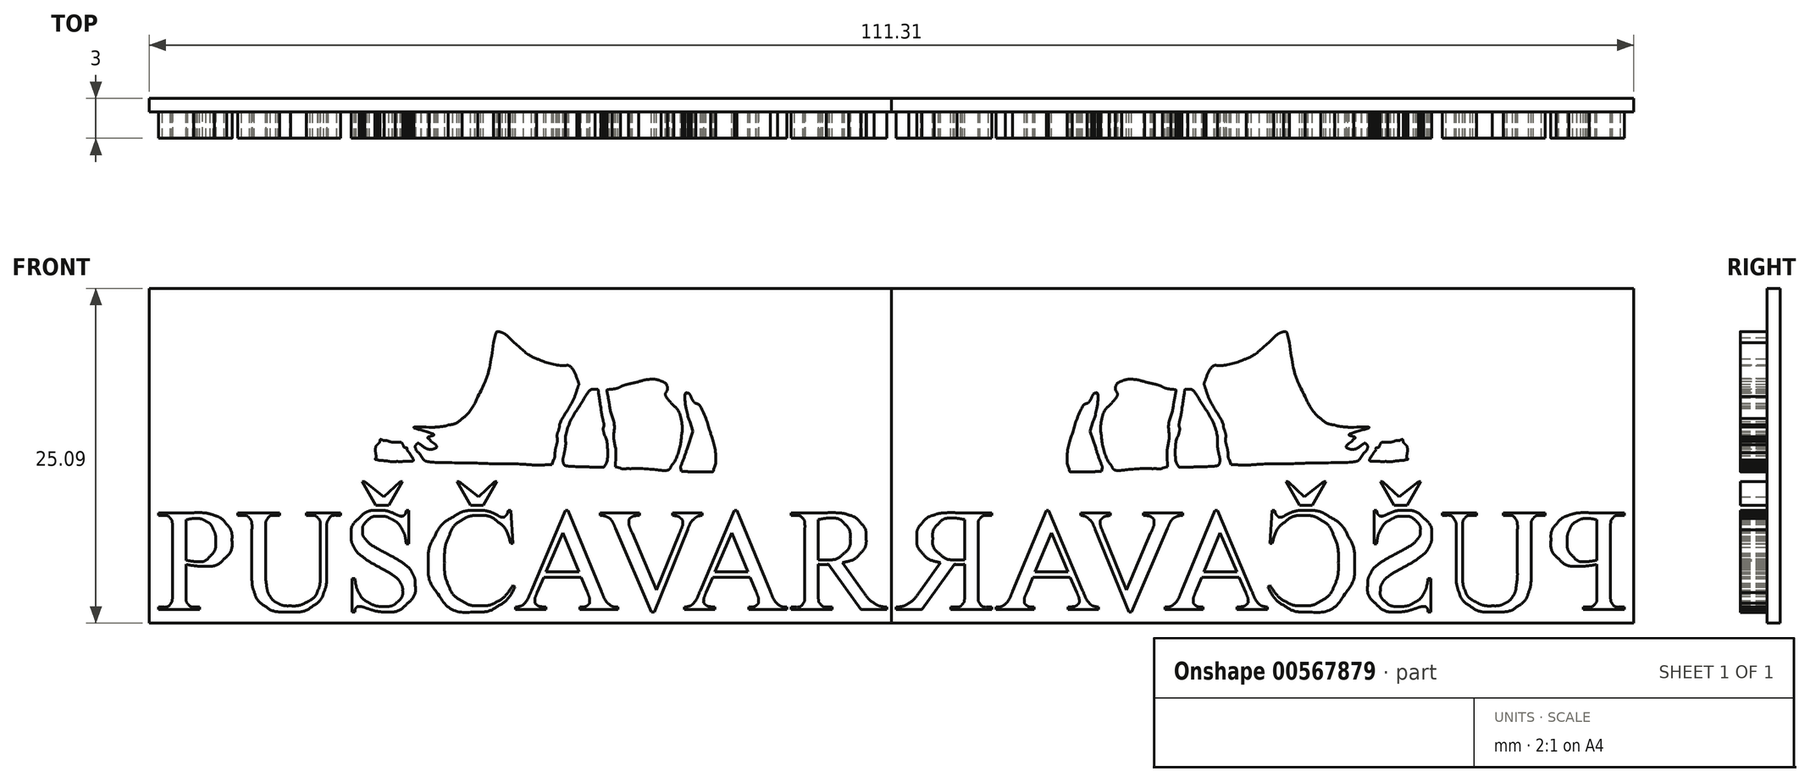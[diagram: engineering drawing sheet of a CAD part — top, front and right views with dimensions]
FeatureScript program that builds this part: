
annotation { "Feature Type Name" : "Feature", "Feature Type Description" : "" }
export const myFeature = defineFeature(function(context is Context, id is Id, definition is map)
    precondition{}
    {
        {
            var Q0;
            Q0=qCreatedBy(makeId("Front.planeOp"),FACE);
            var sketch = newSketch(context, id + "F0", { "sketchPlane" : qUnion([Q0])});
            skFitSpline(sketch, "E0", {"points": [v(14.9, -1.88) * mm, v(14.32, -1.78) * mm, v(13.15, -1.72) * mm, v(11.14, -1.7) * mm]});
            skFitSpline(sketch, "E1", {"points": [v(11.14, -1.7) * mm, v(9.53, -1.67) * mm, v(7.75, -1.61) * mm, v(7.18, -1.56) * mm]});
            skFitSpline(sketch, "E2", {"points": [v(7.18, -1.56) * mm, v(6.6, -1.5) * mm, v(4.27, -1.44) * mm, v(2, -1.41) * mm]});
            skFitSpline(sketch, "E3", {"points": [v(2, -1.41) * mm, v(-0.29, -1.38) * mm, v(-2.6, -1.32) * mm, v(-3.16, -1.26) * mm]});
            skFitSpline(sketch, "E4", {"points": [v(-3.16, -1.26) * mm, v(-3.72, -1.21) * mm, v(-6.43, -1.21) * mm, v(-9.2, -1.18) * mm]});
            skFitSpline(sketch, "E5", {"points": [v(-9.2, -1.18) * mm, v(-13.82, -1.47) * mm, v(-16.55, -0.57) * mm, v(-17.95, 0.52) * mm]});
            skFitSpline(sketch, "E6", {"points": [v(-17.95, 0.52) * mm, v(-20.19, 1.8) * mm, v(-20.67, 2.48) * mm, v(-22.93, 2.6) * mm]});
            skFitSpline(sketch, "E7", {"points": [v(-22.93, 2.6) * mm, v(-24.75, 2.6) * mm, v(-25.04, 2.34) * mm, v(-27, 1.58) * mm]});
            skFitSpline(sketch, "E8", {"points": [v(-27, 1.58) * mm, v(-25.87, 2.73) * mm, v(-24.51, 3.06) * mm, v(-22.9, 3.24) * mm]});
            skFitSpline(sketch, "E9", {"points": [v(-22.9, 3.24) * mm, v(-20.45, 3.27) * mm, v(-17.5, 1.3) * mm, v(-15.9, 0.65) * mm]});
            skFitSpline(sketch, "E10", {"points": [v(-15.9, 0.65) * mm, v(-14.3, 0) * mm, v(-13.89, 0.1) * mm, v(-12.91, -0.13) * mm]});
            skFitSpline(sketch, "E11", {"points": [v(-12.91, -0.13) * mm, v(-12.7, -0.19) * mm, v(-11.86, -0.25) * mm, v(-11.73, -0.1) * mm]});
            skFitSpline(sketch, "E12", {"points": [v(-11.73, -0.1) * mm, v(-11.64, 0) * mm, v(-11.63, 0.35) * mm, v(-11.68, 1.18) * mm]});
            skFitSpline(sketch, "E13", {"points": [v(-11.68, 1.18) * mm, v(-11.74, 2.22) * mm, v(-11.73, 2.38) * mm, v(-11.53, 3) * mm]});
            skFitSpline(sketch, "E14", {"points": [v(-11.53, 3) * mm, v(-11.4, 3.37) * mm, v(-11.14, 4.02) * mm, v(-10.93, 4.43) * mm]});
            skFitSpline(sketch, "E15", {"points": [v(-10.69, 5.94) * mm, v(-10.76, 6.36) * mm, v(-10.82, 7.09) * mm, v(-10.81, 7.57) * mm]});
            skFitSpline(sketch, "E16", {"points": [v(-10.81, 7.57) * mm, v(-10.8, 8.41) * mm, v(-10.81, 8.44) * mm, v(-11.02, 8.44) * mm]});
            skFitSpline(sketch, "E17", {"points": [v(-11.02, 8.44) * mm, v(-11.17, 8.44) * mm, v(-11.28, 8.55) * mm, v(-11.43, 8.86) * mm]});
            skFitSpline(sketch, "E18", {"points": [v(-11.43, 8.86) * mm, v(-11.54, 9.1) * mm, v(-11.63, 9.34) * mm, v(-11.63, 9.41) * mm]});
            skFitSpline(sketch, "E19", {"points": [v(-11.63, 9.41) * mm, v(-11.63, 9.56) * mm, v(-11.28, 9.9) * mm, v(-11.03, 9.98) * mm]});
            skFitSpline(sketch, "E20", {"points": [v(-11.03, 9.98) * mm, v(-10.63, 10.12) * mm, v(-10.18, 9.52) * mm, v(-10.28, 8.99) * mm]});
            skFitSpline(sketch, "E21", {"points": [v(-10.28, 8.99) * mm, v(-10.32, 8.78) * mm, v(-10.25, 8.66) * mm, v(-9.86, 8.3) * mm]});
            skFitSpline(sketch, "E22", {"points": [v(-9.86, 8.3) * mm, v(-9.2, 7.7) * mm, v(-8.6, 6.3) * mm, v(-8.75, 5.8) * mm]});
            skFitSpline(sketch, "E23", {"points": [v(-8.75, 5.8) * mm, v(-8.79, 5.7) * mm, v(-8.77, 5.61) * mm, v(-8.72, 5.61) * mm]});
            skFitSpline(sketch, "E24", {"points": [v(-8.72, 5.61) * mm, v(-8.67, 5.61) * mm, v(-8.57, 5.38) * mm, v(-8.5, 5.08) * mm]});
            skFitSpline(sketch, "E25", {"points": [v(-8.5, 5.08) * mm, v(-8.44, 4.8) * mm, v(-8.26, 4.37) * mm, v(-8.1, 4.14) * mm]});
            skFitSpline(sketch, "E26", {"points": [v(-8.1, 4.14) * mm, v(-7.95, 3.9) * mm, v(-7.8, 3.58) * mm, v(-7.77, 3.42) * mm]});
            skFitSpline(sketch, "E27", {"points": [v(-7.77, 3.42) * mm, v(-7.72, 3.17) * mm, v(-7.62, 3.13) * mm, v(-7.13, 2.94) * mm]});
            skFitSpline(sketch, "E28", {"points": [v(-7.13, 2.94) * mm, v(-6.82, 2.82) * mm, v(-6.27, 2.96) * mm, v(-6, 2.99) * mm]});
            skFitSpline(sketch, "E29", {"points": [v(-6, 2.99) * mm, v(-5.6, 3.02) * mm, v(-4.84, 3.2) * mm, v(-4.06, 4.8) * mm]});
            skFitSpline(sketch, "E30", {"points": [v(-4.06, 4.8) * mm, v(-3.61, 5.73) * mm, v(-3.42, 6.24) * mm, v(-3.16, 6.99) * mm]});
            skFitSpline(sketch, "E31", {"points": [v(-3.16, 6.99) * mm, v(-2.96, 7.56) * mm, v(-2.8, 8.36) * mm, v(-2.73, 8.7) * mm]});
            skFitSpline(sketch, "E32", {"points": [v(-2.73, 8.7) * mm, v(-2.52, 9.68) * mm, v(-2.41, 9.64) * mm, v(-2.93, 9.69) * mm]});
            skFitSpline(sketch, "E33", {"points": [v(-2.93, 9.69) * mm, v(-3.18, 9.71) * mm, v(-3.48, 9.68) * mm, v(-3.61, 9.61) * mm]});
            skFitSpline(sketch, "E34", {"points": [v(-3.61, 9.61) * mm, v(-3.78, 9.53) * mm, v(-3.9, 9.53) * mm, v(-4.06, 9.6) * mm]});
            skFitSpline(sketch, "E35", {"points": [v(-4.06, 9.6) * mm, v(-4.25, 9.68) * mm, v(-4.27, 9.75) * mm, v(-4.22, 9.99) * mm]});
            skFitSpline(sketch, "E36", {"points": [v(-4.22, 9.99) * mm, v(-4.19, 10.15) * mm, v(-4.12, 10.34) * mm, v(-4.08, 10.42) * mm]});
            skFitSpline(sketch, "E37", {"points": [v(-4.08, 10.42) * mm, v(-3.99, 10.6) * mm, v(-3.04, 11.08) * mm, v(-2.77, 11.08) * mm]});
            skFitSpline(sketch, "E38", {"points": [v(-2.77, 11.08) * mm, v(-2.67, 11.08) * mm, v(-2.42, 11.16) * mm, v(-2.23, 11.27) * mm]});
            skFitSpline(sketch, "E39", {"points": [v(-2.23, 11.27) * mm, v(-1.47, 11.66) * mm, v(-1.37, 11.63) * mm, v(-0.75, 10.87) * mm]});
            skFitSpline(sketch, "E40", {"points": [v(-0.75, 10.87) * mm, v(-0.1, 10.05) * mm, v(0.8, 9.25) * mm, v(1.27, 9.04) * mm]});
            skFitSpline(sketch, "E41", {"points": [v(1.27, 9.04) * mm, v(2.05, 8.7) * mm, v(3.56, 8.93) * mm, v(4.48, 9.53) * mm]});
            skFitSpline(sketch, "E42", {"points": [v(4.48, 9.53) * mm, v(5.16, 9.98) * mm, v(6.19, 11.05) * mm, v(6.25, 11.39) * mm]});
            skFitSpline(sketch, "E43", {"points": [v(6.25, 11.39) * mm, v(6.32, 11.74) * mm, v(6.58, 11.72) * mm, v(6.9, 11.35) * mm]});
            skFitSpline(sketch, "E44", {"points": [v(6.9, 11.35) * mm, v(7.1, 11.1) * mm, v(7.18, 11.06) * mm, v(7.32, 11.15) * mm]});
            skFitSpline(sketch, "E45", {"points": [v(7.32, 11.15) * mm, v(7.43, 11.22) * mm, v(7.88, 11.24) * mm, v(8.7, 11.2) * mm]});
            skFitSpline(sketch, "E46", {"points": [v(8.7, 11.2) * mm, v(9.75, 11.15) * mm, v(9.93, 11.17) * mm, v(10.04, 11.3) * mm]});
            skFitSpline(sketch, "E47", {"points": [v(10.04, 11.3) * mm, v(10.28, 11.59) * mm, v(10.71, 11.43) * mm, v(10.71, 11.06) * mm]});
            skFitSpline(sketch, "E48", {"points": [v(10.71, 11.06) * mm, v(10.71, 10.96) * mm, v(10.81, 10.84) * mm, v(10.93, 10.79) * mm]});
            skFitSpline(sketch, "E49", {"points": [v(10.93, 10.79) * mm, v(11.06, 10.73) * mm, v(11.23, 10.54) * mm, v(11.31, 10.36) * mm]});
            skFitSpline(sketch, "E50", {"points": [v(11.31, 10.36) * mm, v(11.4, 10.18) * mm, v(11.65, 9.83) * mm, v(11.87, 9.6) * mm]});
            skFitSpline(sketch, "E51", {"points": [v(11.87, 9.6) * mm, v(12.53, 8.88) * mm, v(12.96, 8.21) * mm, v(13.3, 7.42) * mm]});
            skFitSpline(sketch, "E52", {"points": [v(13.3, 7.42) * mm, v(13.58, 6.8) * mm, v(13.65, 6.49) * mm, v(13.73, 5.57) * mm]});
            skFitSpline(sketch, "E53", {"points": [v(13.73, 5.57) * mm, v(13.8, 4.85) * mm, v(13.88, 4.35) * mm, v(14, 4.12) * mm]});
            skFitSpline(sketch, "E54", {"points": [v(14, 4.12) * mm, v(14.1, 3.93) * mm, v(14.22, 3.56) * mm, v(14.33, 3.35) * mm]});
            skFitSpline(sketch, "E55", {"points": [v(14.33, 3.35) * mm, v(14.44, 3.11) * mm, v(14.48, 2.89) * mm, v(14.58, 2.72) * mm]});
            skFitSpline(sketch, "E56", {"points": [v(14.58, 2.72) * mm, v(14.74, 2.46) * mm, v(14.75, 2.1) * mm, v(14.95, 1.13) * mm]});
            skFitSpline(sketch, "E57", {"points": [v(14.95, 1.13) * mm, v(15.08, 0.48) * mm, v(15, -0.27) * mm, v(15.09, -0.62) * mm]});
            skLineSegment(sketch, "E58", {"start": v(-10.93, 4.43) * mm, "end": v(-10.56, 5.19) * mm});
            skLineSegment(sketch, "E59", {"start": v(-10.56, 5.19) * mm, "end": v(-10.69, 5.94) * mm});
            skFitSpline(sketch, "E60", {"points": [v(15.75, -1.16) * mm, v(16.12, -1.2) * mm, v(16.68, -1.18) * mm, v(17.24, -1.22) * mm]});
            skFitSpline(sketch, "E61", {"points": [v(17.24, -1.22) * mm, v(17.96, -1.27) * mm, v(18.5, -1.26) * mm, v(19.08, -1.17) * mm]});
            skFitSpline(sketch, "E62", {"points": [v(19.08, -1.17) * mm, v(19.84, -1.05) * mm, v(20.1, -0.95) * mm, v(22.27, 0.16) * mm]});
            skFitSpline(sketch, "E63", {"points": [v(22.27, 0.16) * mm, v(24.47, 1.27) * mm, v(26.34, 2.02) * mm, v(26.66, 1.92) * mm]});
            skFitSpline(sketch, "E64", {"points": [v(26.66, 1.92) * mm, v(25.58, 1.3) * mm, v(25.17, 1.06) * mm, v(24.85, 0.96) * mm]});
            skFitSpline(sketch, "E65", {"points": [v(24.85, 0.96) * mm, v(24.04, 0.58) * mm, v(23.13, 0.07) * mm, v(21.22, -0.88) * mm]});
            skFitSpline(sketch, "E66", {"points": [v(21.22, -0.88) * mm, v(19, -2) * mm, v(18.7, -1.79) * mm, v(17.93, -1.92) * mm]});
            skFitSpline(sketch, "E67", {"points": [v(17.93, -1.92) * mm, v(17.12, -1.92) * mm, v(15.47, -1.91) * mm, v(14.9, -1.88) * mm]});
            skLineSegment(sketch, "E68", {"start": v(15.09, -0.62) * mm, "end": v(15.2, -1.1) * mm});
            skLineSegment(sketch, "E69", {"start": v(15.2, -1.1) * mm, "end": v(15.75, -1.16) * mm});
            skFitSpline(sketch, "E70", {"points": [v(14.33, -0.94) * mm, v(14.48, -0.39) * mm, v(14.38, 0.8) * mm, v(14.11, 1.68) * mm]});
            skFitSpline(sketch, "E71", {"points": [v(14.11, 1.68) * mm, v(13.79, 2.73) * mm, v(13.24, 3.87) * mm, v(12.99, 4) * mm]});
            skFitSpline(sketch, "E72", {"points": [v(12.99, 4) * mm, v(12.89, 4.06) * mm, v(12.74, 4.25) * mm, v(12.65, 4.43) * mm]});
            skFitSpline(sketch, "E73", {"points": [v(12.65, 4.43) * mm, v(12.57, 4.61) * mm, v(12.45, 4.76) * mm, v(12.4, 4.76) * mm]});
            skFitSpline(sketch, "E74", {"points": [v(12.4, 4.76) * mm, v(12.22, 4.76) * mm, v(12.3, 3.38) * mm, v(12.54, 2.64) * mm]});
            skLineSegment(sketch, "E75", {"start": v(14.9, -1.88) * mm, "end": v(14.9, -1.88) * mm});
            skFitSpline(sketch, "E76", {"points": [v(12.34, 0.63) * mm, v(12.1, -0.1) * mm, v(11.87, -0.68) * mm, v(11.84, -0.82) * mm]});
            skLineSegment(sketch, "E77", {"start": v(12.54, 2.64) * mm, "end": v(12.77, 1.93) * mm});
            skLineSegment(sketch, "E78", {"start": v(12.77, 1.93) * mm, "end": v(12.34, 0.63) * mm});
            skFitSpline(sketch, "E79", {"points": [v(12.1, -1.1) * mm, v(12.45, -1.12) * mm, v(13.09, -1.13) * mm, v(13.51, -1.13) * mm]});
            skFitSpline(sketch, "E80", {"points": [v(13.51, -1.13) * mm, v(14.2, -1.13) * mm, v(14.29, -1.1) * mm, v(14.33, -0.94) * mm]});
            skLineSegment(sketch, "E81", {"start": v(11.84, -0.82) * mm, "end": v(11.9, -1.09) * mm});
            skLineSegment(sketch, "E82", {"start": v(11.9, -1.09) * mm, "end": v(12.1, -1.1) * mm});
            skFitSpline(sketch, "E83", {"points": [v(10.97, -0.97) * mm, v(11.07, -0.87) * mm, v(11.12, -0.73) * mm, v(11.22, -0.59) * mm]});
            skFitSpline(sketch, "E84", {"points": [v(11.22, -0.59) * mm, v(11.48, -0.2) * mm, v(11.84, 0.92) * mm, v(11.9, 1.53) * mm]});
            skFitSpline(sketch, "E85", {"points": [v(11.9, 1.53) * mm, v(11.97, 2.23) * mm, v(11.68, 3.45) * mm, v(11.35, 3.81) * mm]});
            skFitSpline(sketch, "E86", {"points": [v(11.35, 3.81) * mm, v(10.95, 4.25) * mm, v(10.7, 4.67) * mm, v(10.75, 4.82) * mm]});
            skFitSpline(sketch, "E87", {"points": [v(10.75, 4.82) * mm, v(10.87, 5.12) * mm, v(10.7, 5.54) * mm, v(10.4, 5.66) * mm]});
            skFitSpline(sketch, "E88", {"points": [v(10.4, 5.66) * mm, v(10.06, 5.79) * mm, v(9.26, 5.77) * mm, v(8.69, 5.62) * mm]});
            skFitSpline(sketch, "E89", {"points": [v(8.69, 5.62) * mm, v(8.48, 5.57) * mm, v(8.14, 5.5) * mm, v(7.93, 5.45) * mm]});
            skFitSpline(sketch, "E90", {"points": [v(7.93, 5.45) * mm, v(7.72, 5.4) * mm, v(7.45, 5.3) * mm, v(7.32, 5.24) * mm]});
            skFitSpline(sketch, "E91", {"points": [v(7.32, 5.24) * mm, v(7.2, 5.17) * mm, v(6.92, 5.1) * mm, v(6.7, 5.07) * mm]});
            skFitSpline(sketch, "E92", {"points": [v(6.7, 5.07) * mm, v(6.5, 5.05) * mm, v(6.33, 5.02) * mm, v(6.32, 5.01) * mm]});
            skFitSpline(sketch, "E93", {"points": [v(6.32, 5.01) * mm, v(6.32, 5) * mm, v(6.4, 4.53) * mm, v(6.5, 3.96) * mm]});
            skFitSpline(sketch, "E94", {"points": [v(6.5, 3.96) * mm, v(6.62, 3.3) * mm, v(6.86, 2.5) * mm, v(6.85, 1.84) * mm]});
            skFitSpline(sketch, "E95", {"points": [v(6.85, 1.84) * mm, v(6.84, 1.27) * mm, v(6.99, 0.5) * mm, v(6.98, 0.08) * mm]});
            skFitSpline(sketch, "E96", {"points": [v(7.32, -0.85) * mm, v(7.5, -0.91) * mm, v(7.71, -0.9) * mm, v(8.09, -0.9) * mm]});
            skFitSpline(sketch, "E97", {"points": [v(8.09, -0.9) * mm, v(9.03, -0.9) * mm, v(10.36, -1.01) * mm, v(10.44, -1.02) * mm]});
            skFitSpline(sketch, "E98", {"points": [v(10.44, -1.02) * mm, v(10.61, -1.05) * mm, v(10.81, -1.02) * mm, v(10.97, -0.97) * mm]});
            skLineSegment(sketch, "E99", {"start": v(6.98, 0.08) * mm, "end": v(6.96, -0.75) * mm});
            skLineSegment(sketch, "E100", {"start": v(6.96, -0.75) * mm, "end": v(7.32, -0.85) * mm});
            skFitSpline(sketch, "E101", {"points": [v(6.18, -0.61) * mm, v(6.33, -0.34) * mm, v(6.3, 1.2) * mm, v(6.15, 1.57) * mm]});
            skFitSpline(sketch, "E102", {"points": [v(6.15, 1.57) * mm, v(6.03, 2.13) * mm, v(6.05, 2.18) * mm, v(6.07, 2.22) * mm]});
            skFitSpline(sketch, "E103", {"points": [v(6.07, 2.22) * mm, v(6.11, 2.37) * mm, v(6.1, 2.38) * mm, v(6.09, 2.47) * mm]});
            skFitSpline(sketch, "E104", {"points": [v(6.09, 2.47) * mm, v(6.07, 2.56) * mm, v(5.95, 3.11) * mm, v(5.86, 3.68) * mm]});
            skFitSpline(sketch, "E105", {"points": [v(5.86, 3.68) * mm, v(5.67, 4.98) * mm, v(5.65, 5.05) * mm, v(5.44, 5.05) * mm]});
            skFitSpline(sketch, "E106", {"points": [v(5.44, 5.05) * mm, v(5.14, 5.05) * mm, v(4.83, 4.71) * mm, v(4.24, 3.76) * mm]});
            skFitSpline(sketch, "E107", {"points": [v(4.24, 3.76) * mm, v(3.64, 2.8) * mm, v(3.23, 1.61) * mm, v(3.22, 1.06) * mm]});
            skFitSpline(sketch, "E108", {"points": [v(3.22, 1.06) * mm, v(3.22, 0.9) * mm, v(3.16, 0.46) * mm, v(3.09, 0.1) * mm]});
            skFitSpline(sketch, "E109", {"points": [v(3.09, 0.1) * mm, v(3.02, -0.27) * mm, v(3.1, -0.59) * mm, v(3.12, -0.61) * mm]});
            skFitSpline(sketch, "E110", {"points": [v(3.12, -0.61) * mm, v(3.16, -0.66) * mm, v(4.56, -0.76) * mm, v(5.5, -0.78) * mm]});
            skFitSpline(sketch, "E111", {"points": [v(5.5, -0.78) * mm, v(6, -0.8) * mm, v(6.1, -0.77) * mm, v(6.18, -0.61) * mm]});
            skLineSegment(sketch, "E112", {"start": v(10.97, -0.97) * mm, "end": v(10.97, -0.97) * mm});
            skFitSpline(sketch, "E113", {"points": [v(-7.05, 1.5) * mm, v(-7.13, 1.4) * mm, v(-7, 1.33) * mm, v(-6.91, 1.18) * mm]});
            skFitSpline(sketch, "E114", {"points": [v(-6.91, 1.18) * mm, v(-6.44, 0.72) * mm, v(-7.06, 0.56) * mm, v(-7.58, 0.87) * mm]});
            skFitSpline(sketch, "E115", {"points": [v(-7.58, 0.87) * mm, v(-7.84, 1.03) * mm, v(-7.86, 1.03) * mm, v(-8.02, 0.87) * mm]});
            skFitSpline(sketch, "E116", {"points": [v(-8.02, 0.87) * mm, v(-8.06, 0.77) * mm, v(-8.05, 0.68) * mm, v(-8.03, 0.6) * mm]});
            skFitSpline(sketch, "E117", {"points": [v(-8.03, 0.6) * mm, v(-7.94, 0.42) * mm, v(-7.78, 0.28) * mm, v(-7.63, 0.08) * mm]});
            skFitSpline(sketch, "E118", {"points": [v(-7.63, 0.08) * mm, v(-7.44, -0.2) * mm, v(-7.3, -0.32) * mm, v(-7.04, -0.37) * mm]});
            skFitSpline(sketch, "E119", {"points": [v(-7.04, -0.37) * mm, v(-6.86, -0.4) * mm, v(-5.3, -0.45) * mm, v(-3.6, -0.47) * mm]});
            skFitSpline(sketch, "E120", {"points": [v(-3.6, -0.47) * mm, v(-2.4, -0.52) * mm, v(-0.8, -0.52) * mm, v(0.23, -0.58) * mm]});
            skFitSpline(sketch, "E121", {"points": [v(0.23, -0.58) * mm, v(0.87, -0.62) * mm, v(1.6, -0.61) * mm, v(2.18, -0.6) * mm]});
            skFitSpline(sketch, "E122", {"points": [v(2.33, -0.23) * mm, v(2.4, -0.04) * mm, v(2.44, 0.43) * mm, v(2.51, 0.8) * mm]});
            skFitSpline(sketch, "E123", {"points": [v(2.51, 0.8) * mm, v(2.6, 1.2) * mm, v(2.58, 1.6) * mm, v(2.66, 1.91) * mm]});
            skFitSpline(sketch, "E124", {"points": [v(2.66, 1.91) * mm, v(2.76, 2.28) * mm, v(2.76, 2.4) * mm, v(3.45, 3.63) * mm]});
            skFitSpline(sketch, "E125", {"points": [v(3.45, 3.63) * mm, v(3.67, 4.02) * mm, v(3.93, 4.6) * mm, v(4.03, 4.9) * mm]});
            skFitSpline(sketch, "E126", {"points": [v(4.03, 4.9) * mm, v(4.21, 5.44) * mm, v(4.22, 5.47) * mm, v(4.06, 5.88) * mm]});
            skFitSpline(sketch, "E127", {"points": [v(4.06, 5.88) * mm, v(3.87, 6.37) * mm, v(3.46, 6.84) * mm, v(3.22, 6.84) * mm]});
            skFitSpline(sketch, "E128", {"points": [v(3.22, 6.84) * mm, v(2.84, 6.84) * mm, v(1.51, 7.16) * mm, v(1.06, 7.36) * mm]});
            skFitSpline(sketch, "E129", {"points": [v(1.06, 7.36) * mm, v(0.58, 7.57) * mm, v(-0.1, 8.1) * mm, v(-1.02, 8.93) * mm]});
            skFitSpline(sketch, "E130", {"points": [v(-1.02, 8.93) * mm, v(-1.28, 9.17) * mm, v(-1.53, 9.3) * mm, v(-1.75, 9.38) * mm]});
            skFitSpline(sketch, "E131", {"points": [v(-1.75, 9.38) * mm, v(-1.92, 9.38) * mm, v(-2, 9.3) * mm, v(-2.18, 8.56) * mm]});
            skFitSpline(sketch, "E132", {"points": [v(-2.18, 8.56) * mm, v(-2.56, 6.34) * mm, v(-2.86, 5.53) * mm, v(-3.35, 4.5) * mm]});
            skFitSpline(sketch, "E133", {"points": [v(-3.35, 4.5) * mm, v(-3.67, 3.86) * mm, v(-4.28, 3.05) * mm, v(-4.53, 2.87) * mm]});
            skFitSpline(sketch, "E134", {"points": [v(-4.53, 2.87) * mm, v(-4.82, 2.61) * mm, v(-5.23, 2.43) * mm, v(-5.58, 2.39) * mm]});
            skFitSpline(sketch, "E135", {"points": [v(-5.58, 2.39) * mm, v(-5.9, 2.29) * mm, v(-6.81, 2.2) * mm, v(-7.02, 2.22) * mm]});
            skFitSpline(sketch, "E136", {"points": [v(-7.02, 2.22) * mm, v(-8.16, 2.17) * mm, v(-6.66, 1.67) * mm, v(-7.05, 1.5) * mm]});
            skLineSegment(sketch, "E137", {"start": v(2.18, -0.6) * mm, "end": v(2.33, -0.23) * mm});
            skFitSpline(sketch, "E138", {"points": [v(-8.91, -0.35) * mm, v(-8.5, -0.34) * mm, v(-8.18, -0.28) * mm, v(-8.37, 0.07) * mm]});
            skFitSpline(sketch, "E139", {"points": [v(-8.37, 0.07) * mm, v(-8.4, 0.15) * mm, v(-8.5, 0.3) * mm, v(-8.6, 0.43) * mm]});
            skFitSpline(sketch, "E140", {"points": [v(-8.6, 0.43) * mm, v(-8.68, 0.54) * mm, v(-8.67, 0.65) * mm, v(-8.78, 0.68) * mm]});
            skFitSpline(sketch, "E141", {"points": [v(-8.78, 0.68) * mm, v(-8.91, 0.72) * mm, v(-8.93, 0.8) * mm, v(-8.99, 0.9) * mm]});
            skFitSpline(sketch, "E142", {"points": [v(-8.99, 0.9) * mm, v(-9.07, 1.05) * mm, v(-9.18, 1.09) * mm, v(-9.54, 1.09) * mm]});
            skFitSpline(sketch, "E143", {"points": [v(-9.54, 1.09) * mm, v(-9.8, 1.09) * mm, v(-10.16, 1.2) * mm, v(-10.4, 1.23) * mm]});
            skFitSpline(sketch, "E144", {"points": [v(-10.4, 1.23) * mm, v(-10.48, 1.24) * mm, v(-10.66, 1.3) * mm, v(-10.72, 1.15) * mm]});
            skFitSpline(sketch, "E145", {"points": [v(-10.72, 1.15) * mm, v(-10.75, 1.06) * mm, v(-10.84, 0.97) * mm, v(-10.91, 0.89) * mm]});
            skFitSpline(sketch, "E146", {"points": [v(-10.91, 0.89) * mm, v(-11, 0.79) * mm, v(-11.05, 0.57) * mm, v(-11.03, 0.28) * mm]});
            skFitSpline(sketch, "E147", {"points": [v(-11.03, 0.28) * mm, v(-11, -0.13) * mm, v(-11.08, -0.18) * mm, v(-10.84, -0.24) * mm]});
            skFitSpline(sketch, "E148", {"points": [v(-10.84, -0.24) * mm, v(-10.7, -0.28) * mm, v(-10.52, -0.28) * mm, v(-10.4, -0.3) * mm]});
            skFitSpline(sketch, "E149", {"points": [v(-10.4, -0.3) * mm, v(-10.15, -0.32) * mm, v(-9.92, -0.36) * mm, v(-9.74, -0.37) * mm]});
            skFitSpline(sketch, "E150", {"points": [v(-9.74, -0.37) * mm, v(-9.64, -0.37) * mm, v(-9.6, -0.36) * mm, v(-9.5, -0.36) * mm]});
            skFitSpline(sketch, "E151", {"points": [v(-9.5, -0.36) * mm, v(-9.39, -0.35) * mm, v(-9.29, -0.36) * mm, v(-8.91, -0.35) * mm]});
            skLineSegment(sketch, "E152", {"start": v(-7.05, 1.5) * mm, "end": v(-7.05, 1.5) * mm});
            skFitSpline(sketch, "E153", {"points": [v(14.9, -1.88) * mm, v(14.32, -1.78) * mm, v(13.15, -1.72) * mm, v(11.14, -1.7) * mm]});
            skFitSpline(sketch, "E154", {"points": [v(11.14, -1.7) * mm, v(9.53, -1.67) * mm, v(7.75, -1.61) * mm, v(7.18, -1.56) * mm]});
            skFitSpline(sketch, "E155", {"points": [v(7.18, -1.56) * mm, v(6.6, -1.5) * mm, v(4.27, -1.44) * mm, v(2, -1.41) * mm]});
            skFitSpline(sketch, "E156", {"points": [v(2, -1.41) * mm, v(-0.29, -1.38) * mm, v(-2.6, -1.32) * mm, v(-3.16, -1.26) * mm]});
            skFitSpline(sketch, "E157", {"points": [v(-3.16, -1.26) * mm, v(-3.72, -1.21) * mm, v(-6.43, -1.21) * mm, v(-9.2, -1.18) * mm]});
            skFitSpline(sketch, "E158", {"points": [v(-9.2, -1.18) * mm, v(-13.82, -1.47) * mm, v(-16.55, -0.57) * mm, v(-17.95, 0.52) * mm]});
            skFitSpline(sketch, "E159", {"points": [v(-17.95, 0.52) * mm, v(-20.19, 1.8) * mm, v(-20.67, 2.48) * mm, v(-22.93, 2.6) * mm]});
            skFitSpline(sketch, "E160", {"points": [v(-22.93, 2.6) * mm, v(-24.75, 2.6) * mm, v(-25.04, 2.34) * mm, v(-27, 1.58) * mm]});
            skFitSpline(sketch, "E161", {"points": [v(-27, 1.58) * mm, v(-25.87, 2.73) * mm, v(-24.51, 3.06) * mm, v(-22.9, 3.24) * mm]});
            skFitSpline(sketch, "E162", {"points": [v(-22.9, 3.24) * mm, v(-20.45, 3.27) * mm, v(-17.5, 1.3) * mm, v(-15.9, 0.65) * mm]});
            skFitSpline(sketch, "E163", {"points": [v(-15.9, 0.65) * mm, v(-14.3, 0) * mm, v(-13.89, 0.1) * mm, v(-12.91, -0.13) * mm]});
            skFitSpline(sketch, "E164", {"points": [v(-12.91, -0.13) * mm, v(-12.7, -0.19) * mm, v(-11.86, -0.25) * mm, v(-11.73, -0.1) * mm]});
            skFitSpline(sketch, "E165", {"points": [v(-11.73, -0.1) * mm, v(-11.64, 0) * mm, v(-11.63, 0.35) * mm, v(-11.68, 1.18) * mm]});
            skFitSpline(sketch, "E166", {"points": [v(-11.68, 1.18) * mm, v(-11.74, 2.22) * mm, v(-11.73, 2.38) * mm, v(-11.53, 3) * mm]});
            skFitSpline(sketch, "E167", {"points": [v(-11.53, 3) * mm, v(-11.4, 3.37) * mm, v(-11.14, 4.02) * mm, v(-10.93, 4.43) * mm]});
            skLineSegment(sketch, "E168", {"start": v(-8.91, -0.35) * mm, "end": v(-8.91, -0.35) * mm});
            skFitSpline(sketch, "E169", {"points": [v(-10.69, 5.94) * mm, v(-10.76, 6.36) * mm, v(-10.82, 7.09) * mm, v(-10.81, 7.57) * mm]});
            skFitSpline(sketch, "E170", {"points": [v(-10.81, 7.57) * mm, v(-10.8, 8.41) * mm, v(-10.81, 8.44) * mm, v(-11.02, 8.44) * mm]});
            skFitSpline(sketch, "E171", {"points": [v(-11.02, 8.44) * mm, v(-11.17, 8.44) * mm, v(-11.28, 8.55) * mm, v(-11.43, 8.86) * mm]});
            skFitSpline(sketch, "E172", {"points": [v(-11.43, 8.86) * mm, v(-11.54, 9.1) * mm, v(-11.63, 9.34) * mm, v(-11.63, 9.41) * mm]});
            skFitSpline(sketch, "E173", {"points": [v(-11.63, 9.41) * mm, v(-11.63, 9.56) * mm, v(-11.28, 9.9) * mm, v(-11.03, 9.98) * mm]});
            skFitSpline(sketch, "E174", {"points": [v(-11.03, 9.98) * mm, v(-10.63, 10.12) * mm, v(-10.18, 9.52) * mm, v(-10.28, 8.99) * mm]});
            skFitSpline(sketch, "E175", {"points": [v(-10.28, 8.99) * mm, v(-10.32, 8.78) * mm, v(-10.25, 8.66) * mm, v(-9.86, 8.3) * mm]});
            skFitSpline(sketch, "E176", {"points": [v(-9.86, 8.3) * mm, v(-9.2, 7.7) * mm, v(-8.6, 6.3) * mm, v(-8.75, 5.8) * mm]});
            skFitSpline(sketch, "E177", {"points": [v(-8.75, 5.8) * mm, v(-8.79, 5.7) * mm, v(-8.77, 5.61) * mm, v(-8.72, 5.61) * mm]});
            skFitSpline(sketch, "E178", {"points": [v(-8.72, 5.61) * mm, v(-8.67, 5.61) * mm, v(-8.57, 5.38) * mm, v(-8.5, 5.08) * mm]});
            skFitSpline(sketch, "E179", {"points": [v(-8.5, 5.08) * mm, v(-8.44, 4.8) * mm, v(-8.26, 4.37) * mm, v(-8.1, 4.14) * mm]});
            skFitSpline(sketch, "E180", {"points": [v(-8.1, 4.14) * mm, v(-7.95, 3.9) * mm, v(-7.8, 3.58) * mm, v(-7.77, 3.42) * mm]});
            skFitSpline(sketch, "E181", {"points": [v(-7.77, 3.42) * mm, v(-7.72, 3.17) * mm, v(-7.62, 3.13) * mm, v(-7.13, 2.94) * mm]});
            skFitSpline(sketch, "E182", {"points": [v(-7.13, 2.94) * mm, v(-6.82, 2.82) * mm, v(-6.27, 2.96) * mm, v(-6, 2.99) * mm]});
            skFitSpline(sketch, "E183", {"points": [v(-6, 2.99) * mm, v(-5.6, 3.02) * mm, v(-4.84, 3.2) * mm, v(-4.06, 4.8) * mm]});
            skFitSpline(sketch, "E184", {"points": [v(-4.06, 4.8) * mm, v(-3.61, 5.73) * mm, v(-3.42, 6.24) * mm, v(-3.16, 6.99) * mm]});
            skFitSpline(sketch, "E185", {"points": [v(-3.16, 6.99) * mm, v(-2.96, 7.56) * mm, v(-2.8, 8.36) * mm, v(-2.73, 8.7) * mm]});
            skFitSpline(sketch, "E186", {"points": [v(-2.73, 8.7) * mm, v(-2.52, 9.68) * mm, v(-2.41, 9.64) * mm, v(-2.93, 9.69) * mm]});
            skFitSpline(sketch, "E187", {"points": [v(-2.93, 9.69) * mm, v(-3.18, 9.71) * mm, v(-3.48, 9.68) * mm, v(-3.61, 9.61) * mm]});
            skFitSpline(sketch, "E188", {"points": [v(-3.61, 9.61) * mm, v(-3.78, 9.53) * mm, v(-3.9, 9.53) * mm, v(-4.06, 9.6) * mm]});
            skFitSpline(sketch, "E189", {"points": [v(-4.06, 9.6) * mm, v(-4.25, 9.68) * mm, v(-4.27, 9.75) * mm, v(-4.22, 9.99) * mm]});
            skFitSpline(sketch, "E190", {"points": [v(-4.22, 9.99) * mm, v(-4.19, 10.15) * mm, v(-4.12, 10.34) * mm, v(-4.08, 10.42) * mm]});
            skFitSpline(sketch, "E191", {"points": [v(-4.08, 10.42) * mm, v(-3.99, 10.6) * mm, v(-3.04, 11.08) * mm, v(-2.77, 11.08) * mm]});
            skFitSpline(sketch, "E192", {"points": [v(-2.77, 11.08) * mm, v(-2.67, 11.08) * mm, v(-2.42, 11.16) * mm, v(-2.23, 11.27) * mm]});
            skFitSpline(sketch, "E193", {"points": [v(-2.23, 11.27) * mm, v(-1.47, 11.66) * mm, v(-1.37, 11.63) * mm, v(-0.75, 10.87) * mm]});
            skFitSpline(sketch, "E194", {"points": [v(-0.75, 10.87) * mm, v(-0.1, 10.05) * mm, v(0.8, 9.25) * mm, v(1.27, 9.04) * mm]});
            skFitSpline(sketch, "E195", {"points": [v(1.27, 9.04) * mm, v(2.05, 8.7) * mm, v(3.56, 8.93) * mm, v(4.48, 9.53) * mm]});
            skFitSpline(sketch, "E196", {"points": [v(4.48, 9.53) * mm, v(5.16, 9.98) * mm, v(6.19, 11.05) * mm, v(6.25, 11.39) * mm]});
            skFitSpline(sketch, "E197", {"points": [v(6.25, 11.39) * mm, v(6.32, 11.74) * mm, v(6.58, 11.72) * mm, v(6.9, 11.35) * mm]});
            skFitSpline(sketch, "E198", {"points": [v(6.9, 11.35) * mm, v(7.1, 11.1) * mm, v(7.18, 11.06) * mm, v(7.32, 11.15) * mm]});
            skFitSpline(sketch, "E199", {"points": [v(7.32, 11.15) * mm, v(7.43, 11.22) * mm, v(7.88, 11.24) * mm, v(8.7, 11.2) * mm]});
            skFitSpline(sketch, "E200", {"points": [v(8.7, 11.2) * mm, v(9.75, 11.15) * mm, v(9.93, 11.17) * mm, v(10.04, 11.3) * mm]});
            skFitSpline(sketch, "E201", {"points": [v(10.04, 11.3) * mm, v(10.28, 11.59) * mm, v(10.71, 11.43) * mm, v(10.71, 11.06) * mm]});
            skFitSpline(sketch, "E202", {"points": [v(10.71, 11.06) * mm, v(10.71, 10.96) * mm, v(10.81, 10.84) * mm, v(10.93, 10.79) * mm]});
            skFitSpline(sketch, "E203", {"points": [v(10.93, 10.79) * mm, v(11.06, 10.73) * mm, v(11.23, 10.54) * mm, v(11.31, 10.36) * mm]});
            skFitSpline(sketch, "E204", {"points": [v(11.31, 10.36) * mm, v(11.4, 10.18) * mm, v(11.65, 9.83) * mm, v(11.87, 9.6) * mm]});
            skFitSpline(sketch, "E205", {"points": [v(11.87, 9.6) * mm, v(12.53, 8.88) * mm, v(12.96, 8.21) * mm, v(13.3, 7.42) * mm]});
            skFitSpline(sketch, "E206", {"points": [v(13.3, 7.42) * mm, v(13.58, 6.8) * mm, v(13.65, 6.49) * mm, v(13.73, 5.57) * mm]});
            skFitSpline(sketch, "E207", {"points": [v(13.73, 5.57) * mm, v(13.8, 4.85) * mm, v(13.88, 4.35) * mm, v(14, 4.12) * mm]});
            skFitSpline(sketch, "E208", {"points": [v(14, 4.12) * mm, v(14.1, 3.93) * mm, v(14.22, 3.56) * mm, v(14.33, 3.35) * mm]});
            skFitSpline(sketch, "E209", {"points": [v(14.33, 3.35) * mm, v(14.44, 3.11) * mm, v(14.48, 2.89) * mm, v(14.58, 2.72) * mm]});
            skFitSpline(sketch, "E210", {"points": [v(14.58, 2.72) * mm, v(14.74, 2.46) * mm, v(14.75, 2.1) * mm, v(14.95, 1.13) * mm]});
            skFitSpline(sketch, "E211", {"points": [v(14.95, 1.13) * mm, v(15.08, 0.48) * mm, v(15, -0.27) * mm, v(15.09, -0.62) * mm]});
            skFitSpline(sketch, "E212", {"points": [v(15.75, -1.16) * mm, v(16.12, -1.2) * mm, v(16.68, -1.18) * mm, v(17.24, -1.22) * mm]});
            skFitSpline(sketch, "E213", {"points": [v(17.24, -1.22) * mm, v(17.96, -1.27) * mm, v(18.5, -1.26) * mm, v(19.08, -1.17) * mm]});
            skFitSpline(sketch, "E214", {"points": [v(19.08, -1.17) * mm, v(19.84, -1.05) * mm, v(20.1, -0.95) * mm, v(22.27, 0.16) * mm]});
            skFitSpline(sketch, "E215", {"points": [v(22.27, 0.16) * mm, v(24.47, 1.27) * mm, v(26.34, 2.02) * mm, v(26.66, 1.92) * mm]});
            skFitSpline(sketch, "E216", {"points": [v(26.66, 1.92) * mm, v(25.58, 1.3) * mm, v(25.17, 1.06) * mm, v(24.85, 0.96) * mm]});
            skFitSpline(sketch, "E217", {"points": [v(24.85, 0.96) * mm, v(24.04, 0.58) * mm, v(23.13, 0.07) * mm, v(21.22, -0.88) * mm]});
            skFitSpline(sketch, "E218", {"points": [v(21.22, -0.88) * mm, v(19, -2) * mm, v(18.7, -1.79) * mm, v(17.93, -1.92) * mm]});
            skFitSpline(sketch, "E219", {"points": [v(17.93, -1.92) * mm, v(17.12, -1.92) * mm, v(15.47, -1.91) * mm, v(14.9, -1.88) * mm]});
            skFitSpline(sketch, "E220", {"points": [v(14.33, -0.94) * mm, v(14.48, -0.39) * mm, v(14.38, 0.8) * mm, v(14.11, 1.68) * mm]});
            skFitSpline(sketch, "E221", {"points": [v(14.11, 1.68) * mm, v(13.79, 2.73) * mm, v(13.24, 3.87) * mm, v(12.99, 4) * mm]});
            skFitSpline(sketch, "E222", {"points": [v(12.99, 4) * mm, v(12.89, 4.06) * mm, v(12.74, 4.25) * mm, v(12.65, 4.43) * mm]});
            skFitSpline(sketch, "E223", {"points": [v(12.65, 4.43) * mm, v(12.57, 4.61) * mm, v(12.45, 4.76) * mm, v(12.4, 4.76) * mm]});
            skFitSpline(sketch, "E224", {"points": [v(12.4, 4.76) * mm, v(12.22, 4.76) * mm, v(12.3, 3.38) * mm, v(12.54, 2.64) * mm]});
            skFitSpline(sketch, "E225", {"points": [v(12.34, 0.63) * mm, v(12.1, -0.1) * mm, v(11.87, -0.68) * mm, v(11.84, -0.82) * mm]});
            skFitSpline(sketch, "E226", {"points": [v(12.1, -1.1) * mm, v(12.45, -1.12) * mm, v(13.09, -1.13) * mm, v(13.51, -1.13) * mm]});
            skFitSpline(sketch, "E227", {"points": [v(13.51, -1.13) * mm, v(14.2, -1.13) * mm, v(14.29, -1.1) * mm, v(14.33, -0.94) * mm]});
            skFitSpline(sketch, "E228", {"points": [v(10.97, -0.97) * mm, v(11.07, -0.87) * mm, v(11.12, -0.73) * mm, v(11.22, -0.59) * mm]});
            skFitSpline(sketch, "E229", {"points": [v(11.22, -0.59) * mm, v(11.48, -0.2) * mm, v(11.84, 0.92) * mm, v(11.9, 1.53) * mm]});
            skFitSpline(sketch, "E230", {"points": [v(11.9, 1.53) * mm, v(11.97, 2.23) * mm, v(11.68, 3.45) * mm, v(11.35, 3.81) * mm]});
            skFitSpline(sketch, "E231", {"points": [v(11.35, 3.81) * mm, v(10.95, 4.25) * mm, v(10.7, 4.67) * mm, v(10.75, 4.82) * mm]});
            skFitSpline(sketch, "E232", {"points": [v(10.75, 4.82) * mm, v(10.87, 5.12) * mm, v(10.7, 5.54) * mm, v(10.4, 5.66) * mm]});
            skFitSpline(sketch, "E233", {"points": [v(10.4, 5.66) * mm, v(10.06, 5.79) * mm, v(9.26, 5.77) * mm, v(8.69, 5.62) * mm]});
            skFitSpline(sketch, "E234", {"points": [v(8.69, 5.62) * mm, v(8.48, 5.57) * mm, v(8.14, 5.5) * mm, v(7.93, 5.45) * mm]});
            skFitSpline(sketch, "E235", {"points": [v(7.93, 5.45) * mm, v(7.72, 5.4) * mm, v(7.45, 5.3) * mm, v(7.32, 5.24) * mm]});
            skFitSpline(sketch, "E236", {"points": [v(7.32, 5.24) * mm, v(7.2, 5.17) * mm, v(6.92, 5.1) * mm, v(6.7, 5.07) * mm]});
            skFitSpline(sketch, "E237", {"points": [v(6.7, 5.07) * mm, v(6.5, 5.05) * mm, v(6.33, 5.02) * mm, v(6.32, 5.01) * mm]});
            skFitSpline(sketch, "E238", {"points": [v(6.32, 5.01) * mm, v(6.32, 5) * mm, v(6.4, 4.53) * mm, v(6.5, 3.96) * mm]});
            skFitSpline(sketch, "E239", {"points": [v(6.5, 3.96) * mm, v(6.62, 3.3) * mm, v(6.86, 2.5) * mm, v(6.85, 1.84) * mm]});
            skFitSpline(sketch, "E240", {"points": [v(6.85, 1.84) * mm, v(6.84, 1.27) * mm, v(6.99, 0.5) * mm, v(6.98, 0.08) * mm]});
            skFitSpline(sketch, "E241", {"points": [v(7.32, -0.85) * mm, v(7.5, -0.91) * mm, v(7.71, -0.9) * mm, v(8.09, -0.9) * mm]});
            skFitSpline(sketch, "E242", {"points": [v(8.09, -0.9) * mm, v(9.03, -0.9) * mm, v(10.36, -1.01) * mm, v(10.44, -1.02) * mm]});
            skFitSpline(sketch, "E243", {"points": [v(10.44, -1.02) * mm, v(10.61, -1.05) * mm, v(10.81, -1.02) * mm, v(10.97, -0.97) * mm]});
            skFitSpline(sketch, "E244", {"points": [v(6.18, -0.61) * mm, v(6.33, -0.34) * mm, v(6.3, 1.2) * mm, v(6.15, 1.57) * mm]});
            skFitSpline(sketch, "E245", {"points": [v(6.15, 1.57) * mm, v(6.03, 2.13) * mm, v(6.05, 2.18) * mm, v(6.07, 2.22) * mm]});
            skFitSpline(sketch, "E246", {"points": [v(6.07, 2.22) * mm, v(6.11, 2.37) * mm, v(6.1, 2.38) * mm, v(6.09, 2.47) * mm]});
            skFitSpline(sketch, "E247", {"points": [v(6.09, 2.47) * mm, v(6.07, 2.56) * mm, v(5.95, 3.11) * mm, v(5.86, 3.68) * mm]});
            skFitSpline(sketch, "E248", {"points": [v(5.86, 3.68) * mm, v(5.67, 4.98) * mm, v(5.65, 5.05) * mm, v(5.44, 5.05) * mm]});
            skFitSpline(sketch, "E249", {"points": [v(5.44, 5.05) * mm, v(5.14, 5.05) * mm, v(4.83, 4.71) * mm, v(4.24, 3.76) * mm]});
            skFitSpline(sketch, "E250", {"points": [v(4.24, 3.76) * mm, v(3.64, 2.8) * mm, v(3.23, 1.61) * mm, v(3.22, 1.06) * mm]});
            skFitSpline(sketch, "E251", {"points": [v(3.22, 1.06) * mm, v(3.22, 0.9) * mm, v(3.16, 0.46) * mm, v(3.09, 0.1) * mm]});
            skFitSpline(sketch, "E252", {"points": [v(3.09, 0.1) * mm, v(3.02, -0.27) * mm, v(3.1, -0.59) * mm, v(3.12, -0.61) * mm]});
            skFitSpline(sketch, "E253", {"points": [v(3.12, -0.61) * mm, v(3.16, -0.66) * mm, v(4.56, -0.76) * mm, v(5.5, -0.78) * mm]});
            skFitSpline(sketch, "E254", {"points": [v(5.5, -0.78) * mm, v(6, -0.8) * mm, v(6.1, -0.77) * mm, v(6.18, -0.61) * mm]});
            skFitSpline(sketch, "E255", {"points": [v(-7.05, 1.5) * mm, v(-7.13, 1.4) * mm, v(-7, 1.33) * mm, v(-6.91, 1.18) * mm]});
            skFitSpline(sketch, "E256", {"points": [v(-6.91, 1.18) * mm, v(-6.44, 0.72) * mm, v(-7.06, 0.56) * mm, v(-7.58, 0.87) * mm]});
            skFitSpline(sketch, "E257", {"points": [v(-7.58, 0.87) * mm, v(-7.84, 1.03) * mm, v(-7.86, 1.03) * mm, v(-8.02, 0.87) * mm]});
            skFitSpline(sketch, "E258", {"points": [v(-8.02, 0.87) * mm, v(-8.06, 0.77) * mm, v(-8.05, 0.68) * mm, v(-8.03, 0.6) * mm]});
            skFitSpline(sketch, "E259", {"points": [v(-8.03, 0.6) * mm, v(-7.94, 0.42) * mm, v(-7.78, 0.28) * mm, v(-7.63, 0.08) * mm]});
            skFitSpline(sketch, "E260", {"points": [v(-7.63, 0.08) * mm, v(-7.44, -0.2) * mm, v(-7.3, -0.32) * mm, v(-7.04, -0.37) * mm]});
            skFitSpline(sketch, "E261", {"points": [v(-7.04, -0.37) * mm, v(-6.86, -0.4) * mm, v(-5.3, -0.45) * mm, v(-3.6, -0.47) * mm]});
            skFitSpline(sketch, "E262", {"points": [v(-3.6, -0.47) * mm, v(-2.4, -0.52) * mm, v(-0.8, -0.52) * mm, v(0.23, -0.58) * mm]});
            skFitSpline(sketch, "E263", {"points": [v(0.23, -0.58) * mm, v(0.87, -0.62) * mm, v(1.6, -0.61) * mm, v(2.18, -0.6) * mm]});
            skFitSpline(sketch, "E264", {"points": [v(2.33, -0.23) * mm, v(2.4, -0.04) * mm, v(2.44, 0.43) * mm, v(2.51, 0.8) * mm]});
            skFitSpline(sketch, "E265", {"points": [v(2.51, 0.8) * mm, v(2.6, 1.2) * mm, v(2.58, 1.6) * mm, v(2.66, 1.91) * mm]});
            skFitSpline(sketch, "E266", {"points": [v(2.66, 1.91) * mm, v(2.76, 2.28) * mm, v(2.76, 2.4) * mm, v(3.45, 3.63) * mm]});
            skFitSpline(sketch, "E267", {"points": [v(3.45, 3.63) * mm, v(3.67, 4.02) * mm, v(3.93, 4.6) * mm, v(4.03, 4.9) * mm]});
            skFitSpline(sketch, "E268", {"points": [v(4.03, 4.9) * mm, v(4.21, 5.44) * mm, v(4.22, 5.47) * mm, v(4.06, 5.88) * mm]});
            skFitSpline(sketch, "E269", {"points": [v(4.06, 5.88) * mm, v(3.87, 6.37) * mm, v(3.46, 6.84) * mm, v(3.22, 6.84) * mm]});
            skFitSpline(sketch, "E270", {"points": [v(3.22, 6.84) * mm, v(2.84, 6.84) * mm, v(1.51, 7.16) * mm, v(1.06, 7.36) * mm]});
            skFitSpline(sketch, "E271", {"points": [v(1.06, 7.36) * mm, v(0.58, 7.57) * mm, v(-0.1, 8.1) * mm, v(-1.02, 8.93) * mm]});
            skFitSpline(sketch, "E272", {"points": [v(-1.02, 8.93) * mm, v(-1.28, 9.17) * mm, v(-1.53, 9.3) * mm, v(-1.75, 9.38) * mm]});
            skFitSpline(sketch, "E273", {"points": [v(-1.75, 9.38) * mm, v(-1.92, 9.38) * mm, v(-2, 9.3) * mm, v(-2.18, 8.56) * mm]});
            skFitSpline(sketch, "E274", {"points": [v(-2.18, 8.56) * mm, v(-2.56, 6.34) * mm, v(-2.86, 5.53) * mm, v(-3.35, 4.5) * mm]});
            skFitSpline(sketch, "E275", {"points": [v(-3.35, 4.5) * mm, v(-3.67, 3.86) * mm, v(-4.28, 3.05) * mm, v(-4.53, 2.87) * mm]});
            skFitSpline(sketch, "E276", {"points": [v(-4.53, 2.87) * mm, v(-4.82, 2.61) * mm, v(-5.23, 2.43) * mm, v(-5.58, 2.39) * mm]});
            skFitSpline(sketch, "E277", {"points": [v(-5.58, 2.39) * mm, v(-5.9, 2.29) * mm, v(-6.81, 2.2) * mm, v(-7.02, 2.22) * mm]});
            skFitSpline(sketch, "E278", {"points": [v(-7.02, 2.22) * mm, v(-8.16, 2.17) * mm, v(-6.66, 1.67) * mm, v(-7.05, 1.5) * mm]});
            skFitSpline(sketch, "E279", {"points": [v(-8.91, -0.35) * mm, v(-8.5, -0.34) * mm, v(-8.18, -0.28) * mm, v(-8.37, 0.07) * mm]});
            skFitSpline(sketch, "E280", {"points": [v(-8.37, 0.07) * mm, v(-8.4, 0.15) * mm, v(-8.5, 0.3) * mm, v(-8.6, 0.43) * mm]});
            skFitSpline(sketch, "E281", {"points": [v(-8.6, 0.43) * mm, v(-8.68, 0.54) * mm, v(-8.67, 0.65) * mm, v(-8.78, 0.68) * mm]});
            skFitSpline(sketch, "E282", {"points": [v(-8.78, 0.68) * mm, v(-8.91, 0.72) * mm, v(-8.93, 0.8) * mm, v(-8.99, 0.9) * mm]});
            skFitSpline(sketch, "E283", {"points": [v(-8.99, 0.9) * mm, v(-9.07, 1.05) * mm, v(-9.18, 1.09) * mm, v(-9.54, 1.09) * mm]});
            skFitSpline(sketch, "E284", {"points": [v(-9.54, 1.09) * mm, v(-9.8, 1.09) * mm, v(-10.16, 1.2) * mm, v(-10.4, 1.23) * mm]});
            skFitSpline(sketch, "E285", {"points": [v(-10.4, 1.23) * mm, v(-10.48, 1.24) * mm, v(-10.66, 1.3) * mm, v(-10.72, 1.15) * mm]});
            skFitSpline(sketch, "E286", {"points": [v(-10.72, 1.15) * mm, v(-10.75, 1.06) * mm, v(-10.84, 0.97) * mm, v(-10.91, 0.89) * mm]});
            skFitSpline(sketch, "E287", {"points": [v(-10.91, 0.89) * mm, v(-11, 0.79) * mm, v(-11.05, 0.57) * mm, v(-11.03, 0.28) * mm]});
            skFitSpline(sketch, "E288", {"points": [v(-11.03, 0.28) * mm, v(-11, -0.13) * mm, v(-11.08, -0.18) * mm, v(-10.84, -0.24) * mm]});
            skFitSpline(sketch, "E289", {"points": [v(-10.84, -0.24) * mm, v(-10.7, -0.28) * mm, v(-10.52, -0.28) * mm, v(-10.4, -0.3) * mm]});
            skFitSpline(sketch, "E290", {"points": [v(-10.4, -0.3) * mm, v(-10.15, -0.32) * mm, v(-9.92, -0.36) * mm, v(-9.74, -0.37) * mm]});
            skFitSpline(sketch, "E291", {"points": [v(-9.74, -0.37) * mm, v(-9.64, -0.37) * mm, v(-9.6, -0.36) * mm, v(-9.5, -0.36) * mm]});
            skFitSpline(sketch, "E292", {"points": [v(-9.5, -0.36) * mm, v(-9.39, -0.35) * mm, v(-9.29, -0.36) * mm, v(-8.91, -0.35) * mm]});
            skFitSpline(sketch, "E293", {"points": [v(-25.25, -10.18) * mm, v(-25.25, -10.64) * mm, v(-25.2, -10.92) * mm, v(-25.1, -11.03) * mm]});
            skFitSpline(sketch, "E294", {"points": [v(-25.1, -11.03) * mm, v(-24.96, -11.19) * mm, v(-24.76, -11.27) * mm, v(-24.49, -11.27) * mm]});
            skLineSegment(sketch, "E295", {"start": v(-25.25, -8.06) * mm, "end": v(-25.25, -10.18) * mm});
            skFitSpline(sketch, "E296", {"points": [v(-27.03, -11.27) * mm, v(-26.73, -11.27) * mm, v(-26.5, -11.17) * mm, v(-26.38, -10.97) * mm]});
            skFitSpline(sketch, "E297", {"points": [v(-26.38, -10.97) * mm, v(-26.3, -10.86) * mm, v(-26.27, -10.6) * mm, v(-26.27, -10.18) * mm]});
            skLineSegment(sketch, "E298", {"start": v(-24.49, -11.27) * mm, "end": v(-24.2, -11.27) * mm});
            skLineSegment(sketch, "E299", {"start": v(-24.2, -11.27) * mm, "end": v(-24.2, -11.47) * mm});
            skLineSegment(sketch, "E300", {"start": v(-24.2, -11.47) * mm, "end": v(-27.3, -11.47) * mm});
            skLineSegment(sketch, "E301", {"start": v(-27.3, -11.47) * mm, "end": v(-27.3, -11.27) * mm});
            skLineSegment(sketch, "E302", {"start": v(-27.3, -11.27) * mm, "end": v(-27.03, -11.27) * mm});
            skFitSpline(sketch, "E303", {"points": [v(-26.27, -5.48) * mm, v(-26.27, -5.03) * mm, v(-26.32, -4.74) * mm, v(-26.41, -4.63) * mm]});
            skFitSpline(sketch, "E304", {"points": [v(-26.41, -4.63) * mm, v(-26.55, -4.48) * mm, v(-26.76, -4.4) * mm, v(-27.03, -4.4) * mm]});
            skLineSegment(sketch, "E305", {"start": v(-26.27, -10.18) * mm, "end": v(-26.27, -5.48) * mm});
            skFitSpline(sketch, "E306", {"points": [v(-24.66, -4.2) * mm, v(-24.01, -4.2) * mm, v(-23.5, -4.27) * mm, v(-23.13, -4.4) * mm]});
            skFitSpline(sketch, "E307", {"points": [v(-23.13, -4.4) * mm, v(-22.76, -4.53) * mm, v(-22.44, -4.76) * mm, v(-22.19, -5.08) * mm]});
            skFitSpline(sketch, "E308", {"points": [v(-22.19, -5.08) * mm, v(-21.93, -5.4) * mm, v(-21.8, -5.77) * mm, v(-21.8, -6.2) * mm]});
            skFitSpline(sketch, "E309", {"points": [v(-21.8, -6.2) * mm, v(-21.8, -6.8) * mm, v(-22, -7.28) * mm, v(-22.39, -7.66) * mm]});
            skFitSpline(sketch, "E310", {"points": [v(-22.39, -7.66) * mm, v(-22.77, -8.03) * mm, v(-23.32, -8.21) * mm, v(-24.03, -8.21) * mm]});
            skFitSpline(sketch, "E311", {"points": [v(-24.03, -8.21) * mm, v(-24.2, -8.21) * mm, v(-24.4, -8.2) * mm, v(-24.6, -8.18) * mm]});
            skFitSpline(sketch, "E312", {"points": [v(-24.6, -8.18) * mm, v(-24.8, -8.15) * mm, v(-25.02, -8.11) * mm, v(-25.25, -8.06) * mm]});
            skLineSegment(sketch, "E313", {"start": v(-27.03, -4.4) * mm, "end": v(-27.3, -4.4) * mm});
            skLineSegment(sketch, "E314", {"start": v(-27.3, -4.4) * mm, "end": v(-27.3, -4.2) * mm});
            skLineSegment(sketch, "E315", {"start": v(-27.3, -4.2) * mm, "end": v(-24.66, -4.2) * mm});
            skFitSpline(sketch, "E316", {"points": [v(-25.25, -7.76) * mm, v(-25.06, -7.8) * mm, v(-24.9, -7.82) * mm, v(-24.75, -7.84) * mm]});
            skFitSpline(sketch, "E317", {"points": [v(-24.75, -7.84) * mm, v(-24.6, -7.86) * mm, v(-24.48, -7.86) * mm, v(-24.37, -7.86) * mm]});
            skFitSpline(sketch, "E318", {"points": [v(-24.37, -7.86) * mm, v(-24, -7.86) * mm, v(-23.69, -7.72) * mm, v(-23.42, -7.43) * mm]});
            skFitSpline(sketch, "E319", {"points": [v(-23.42, -7.43) * mm, v(-23.15, -7.15) * mm, v(-23.02, -6.77) * mm, v(-23.02, -6.32) * mm]});
            skFitSpline(sketch, "E320", {"points": [v(-23.02, -6.32) * mm, v(-23.02, -6) * mm, v(-23.08, -5.7) * mm, v(-23.2, -5.44) * mm]});
            skFitSpline(sketch, "E321", {"points": [v(-23.2, -5.44) * mm, v(-23.34, -5.17) * mm, v(-23.52, -4.97) * mm, v(-23.75, -4.83) * mm]});
            skFitSpline(sketch, "E322", {"points": [v(-23.75, -4.83) * mm, v(-23.99, -4.7) * mm, v(-24.25, -4.63) * mm, v(-24.55, -4.63) * mm]});
            skFitSpline(sketch, "E323", {"points": [v(-24.55, -4.63) * mm, v(-24.73, -4.63) * mm, v(-24.96, -4.67) * mm, v(-25.25, -4.73) * mm]});
            skLineSegment(sketch, "E324", {"start": v(-25.25, -4.73) * mm, "end": v(-25.25, -7.76) * mm});
            skFitSpline(sketch, "E325", {"points": [v(-13.93, -4.4) * mm, v(-14.21, -4.4) * mm, v(-14.43, -4.52) * mm, v(-14.58, -4.76) * mm]});
            skFitSpline(sketch, "E326", {"points": [v(-14.58, -4.76) * mm, v(-14.66, -4.87) * mm, v(-14.7, -5.12) * mm, v(-14.7, -5.53) * mm]});
            skLineSegment(sketch, "E327", {"start": v(-16.21, -4.4) * mm, "end": v(-16.21, -4.2) * mm});
            skLineSegment(sketch, "E328", {"start": v(-16.21, -4.2) * mm, "end": v(-13.66, -4.2) * mm});
            skLineSegment(sketch, "E329", {"start": v(-13.66, -4.2) * mm, "end": v(-13.66, -4.4) * mm});
            skLineSegment(sketch, "E330", {"start": v(-13.66, -4.4) * mm, "end": v(-13.93, -4.4) * mm});
            skFitSpline(sketch, "E331", {"points": [v(-14.7, -8.48) * mm, v(-14.7, -9.2) * mm, v(-14.77, -9.77) * mm, v(-14.91, -10.17) * mm]});
            skFitSpline(sketch, "E332", {"points": [v(-14.91, -10.17) * mm, v(-15.05, -10.57) * mm, v(-15.34, -10.92) * mm, v(-15.76, -11.2) * mm]});
            skFitSpline(sketch, "E333", {"points": [v(-15.76, -11.2) * mm, v(-16.18, -11.5) * mm, v(-16.75, -11.64) * mm, v(-17.47, -11.64) * mm]});
            skFitSpline(sketch, "E334", {"points": [v(-17.47, -11.64) * mm, v(-18.26, -11.64) * mm, v(-18.86, -11.5) * mm, v(-19.27, -11.23) * mm]});
            skFitSpline(sketch, "E335", {"points": [v(-19.27, -11.23) * mm, v(-19.68, -10.95) * mm, v(-19.97, -10.58) * mm, v(-20.14, -10.12) * mm]});
            skFitSpline(sketch, "E336", {"points": [v(-20.14, -10.12) * mm, v(-20.25, -9.8) * mm, v(-20.3, -9.2) * mm, v(-20.3, -8.33) * mm]});
            skLineSegment(sketch, "E337", {"start": v(-14.7, -5.53) * mm, "end": v(-14.7, -8.48) * mm});
            skFitSpline(sketch, "E338", {"points": [v(-20.3, -5.48) * mm, v(-20.3, -5.04) * mm, v(-20.37, -4.75) * mm, v(-20.5, -4.6) * mm]});
            skFitSpline(sketch, "E339", {"points": [v(-20.5, -4.6) * mm, v(-20.61, -4.47) * mm, v(-20.81, -4.4) * mm, v(-21.08, -4.4) * mm]});
            skLineSegment(sketch, "E340", {"start": v(-20.3, -8.33) * mm, "end": v(-20.3, -5.48) * mm});
            skFitSpline(sketch, "E341", {"points": [v(-18.51, -4.4) * mm, v(-18.81, -4.4) * mm, v(-19.02, -4.5) * mm, v(-19.15, -4.68) * mm]});
            skFitSpline(sketch, "E342", {"points": [v(-19.15, -4.68) * mm, v(-19.24, -4.8) * mm, v(-19.28, -5.08) * mm, v(-19.28, -5.48) * mm]});
            skLineSegment(sketch, "E343", {"start": v(-21.08, -4.4) * mm, "end": v(-21.36, -4.4) * mm});
            skLineSegment(sketch, "E344", {"start": v(-21.36, -4.4) * mm, "end": v(-21.36, -4.2) * mm});
            skLineSegment(sketch, "E345", {"start": v(-21.36, -4.2) * mm, "end": v(-18.24, -4.2) * mm});
            skLineSegment(sketch, "E346", {"start": v(-18.24, -4.2) * mm, "end": v(-18.24, -4.4) * mm});
            skLineSegment(sketch, "E347", {"start": v(-18.24, -4.4) * mm, "end": v(-18.51, -4.4) * mm});
            skFitSpline(sketch, "E348", {"points": [v(-19.28, -8.65) * mm, v(-19.28, -8.93) * mm, v(-19.26, -9.26) * mm, v(-19.2, -9.62) * mm]});
            skFitSpline(sketch, "E349", {"points": [v(-19.2, -9.62) * mm, v(-19.16, -9.99) * mm, v(-19.06, -10.27) * mm, v(-18.93, -10.48) * mm]});
            skFitSpline(sketch, "E350", {"points": [v(-18.93, -10.48) * mm, v(-18.8, -10.68) * mm, v(-18.6, -10.85) * mm, v(-18.34, -10.98) * mm]});
            skFitSpline(sketch, "E351", {"points": [v(-18.34, -10.98) * mm, v(-18.1, -11.11) * mm, v(-17.78, -11.18) * mm, v(-17.4, -11.18) * mm]});
            skFitSpline(sketch, "E352", {"points": [v(-17.4, -11.18) * mm, v(-16.94, -11.18) * mm, v(-16.52, -11.07) * mm, v(-16.14, -10.87) * mm]});
            skFitSpline(sketch, "E353", {"points": [v(-16.14, -10.87) * mm, v(-15.77, -10.66) * mm, v(-15.52, -10.4) * mm, v(-15.38, -10.07) * mm]});
            skFitSpline(sketch, "E354", {"points": [v(-15.38, -10.07) * mm, v(-15.24, -9.75) * mm, v(-15.17, -9.2) * mm, v(-15.17, -8.43) * mm]});
            skLineSegment(sketch, "E355", {"start": v(-19.28, -5.48) * mm, "end": v(-19.28, -8.65) * mm});
            skFitSpline(sketch, "E356", {"points": [v(-15.17, -5.48) * mm, v(-15.17, -5.03) * mm, v(-15.22, -4.75) * mm, v(-15.32, -4.63) * mm]});
            skFitSpline(sketch, "E357", {"points": [v(-15.32, -4.63) * mm, v(-15.46, -4.48) * mm, v(-15.67, -4.4) * mm, v(-15.94, -4.4) * mm]});
            skLineSegment(sketch, "E358", {"start": v(-15.17, -8.43) * mm, "end": v(-15.17, -5.48) * mm});
            skLineSegment(sketch, "E359", {"start": v(-15.94, -4.4) * mm, "end": v(-16.21, -4.4) * mm});
            skFitSpline(sketch, "E360", {"points": [v(-8.73, -6.55) * mm, v(-8.8, -6.06) * mm, v(-8.9, -5.68) * mm, v(-9.07, -5.4) * mm]});
            skFitSpline(sketch, "E361", {"points": [v(-9.07, -5.4) * mm, v(-9.24, -5.1) * mm, v(-9.47, -4.88) * mm, v(-9.78, -4.71) * mm]});
            skFitSpline(sketch, "E362", {"points": [v(-9.78, -4.71) * mm, v(-10.09, -4.54) * mm, v(-10.4, -4.46) * mm, v(-10.73, -4.46) * mm]});
            skFitSpline(sketch, "E363", {"points": [v(-10.73, -4.46) * mm, v(-11.1, -4.46) * mm, v(-11.4, -4.57) * mm, v(-11.64, -4.8) * mm]});
            skFitSpline(sketch, "E364", {"points": [v(-11.64, -4.8) * mm, v(-11.88, -5.03) * mm, v(-12, -5.29) * mm, v(-12, -5.58) * mm]});
            skFitSpline(sketch, "E365", {"points": [v(-12, -5.58) * mm, v(-12, -5.8) * mm, v(-11.93, -6) * mm, v(-11.78, -6.18) * mm]});
            skFitSpline(sketch, "E366", {"points": [v(-11.78, -6.18) * mm, v(-11.56, -6.45) * mm, v(-11.03, -6.8) * mm, v(-10.2, -7.25) * mm]});
            skFitSpline(sketch, "E367", {"points": [v(-10.2, -7.25) * mm, v(-9.53, -7.62) * mm, v(-9.07, -7.9) * mm, v(-8.82, -8.1) * mm]});
            skFitSpline(sketch, "E368", {"points": [v(-8.82, -8.1) * mm, v(-8.58, -8.29) * mm, v(-8.39, -8.52) * mm, v(-8.25, -8.78) * mm]});
            skFitSpline(sketch, "E369", {"points": [v(-8.25, -8.78) * mm, v(-8.12, -9.05) * mm, v(-8.05, -9.32) * mm, v(-8.05, -9.61) * mm]});
            skFitSpline(sketch, "E370", {"points": [v(-8.05, -9.61) * mm, v(-8.05, -10.16) * mm, v(-8.27, -10.64) * mm, v(-8.7, -11.04) * mm]});
            skFitSpline(sketch, "E371", {"points": [v(-8.7, -11.04) * mm, v(-9.12, -11.43) * mm, v(-9.66, -11.63) * mm, v(-10.33, -11.63) * mm]});
            skFitSpline(sketch, "E372", {"points": [v(-10.33, -11.63) * mm, v(-10.54, -11.63) * mm, v(-10.73, -11.62) * mm, v(-10.92, -11.58) * mm]});
            skFitSpline(sketch, "E373", {"points": [v(-10.92, -11.58) * mm, v(-11.03, -11.57) * mm, v(-11.26, -11.5) * mm, v(-11.6, -11.39) * mm]});
            skFitSpline(sketch, "E374", {"points": [v(-11.6, -11.39) * mm, v(-11.95, -11.28) * mm, v(-12.17, -11.22) * mm, v(-12.26, -11.22) * mm]});
            skFitSpline(sketch, "E375", {"points": [v(-12.26, -11.22) * mm, v(-12.35, -11.22) * mm, v(-12.42, -11.25) * mm, v(-12.47, -11.3) * mm]});
            skFitSpline(sketch, "E376", {"points": [v(-12.47, -11.3) * mm, v(-12.52, -11.35) * mm, v(-12.56, -11.46) * mm, v(-12.59, -11.63) * mm]});
            skLineSegment(sketch, "E377", {"start": v(-8.53, -4.03) * mm, "end": v(-8.53, -6.55) * mm});
            skLineSegment(sketch, "E378", {"start": v(-8.53, -6.55) * mm, "end": v(-8.73, -6.55) * mm});
            skFitSpline(sketch, "E379", {"points": [v(-12.59, -9.14) * mm, v(-12.5, -9.66) * mm, v(-12.37, -10.05) * mm, v(-12.21, -10.31) * mm]});
            skFitSpline(sketch, "E380", {"points": [v(-12.21, -10.31) * mm, v(-12.06, -10.57) * mm, v(-11.82, -10.79) * mm, v(-11.5, -10.96) * mm]});
            skFitSpline(sketch, "E381", {"points": [v(-11.5, -10.96) * mm, v(-11.18, -11.13) * mm, v(-10.82, -11.21) * mm, v(-10.44, -11.21) * mm]});
            skFitSpline(sketch, "E382", {"points": [v(-10.44, -11.21) * mm, v(-10, -11.21) * mm, v(-9.65, -11.1) * mm, v(-9.39, -10.86) * mm]});
            skFitSpline(sketch, "E383", {"points": [v(-9.39, -10.86) * mm, v(-9.13, -10.63) * mm, v(-9, -10.35) * mm, v(-9, -10.02) * mm]});
            skFitSpline(sketch, "E384", {"points": [v(-9, -10.02) * mm, v(-9, -9.85) * mm, v(-9.05, -9.67) * mm, v(-9.15, -9.48) * mm]});
            skFitSpline(sketch, "E385", {"points": [v(-9.15, -9.48) * mm, v(-9.25, -9.3) * mm, v(-9.4, -9.13) * mm, v(-9.6, -8.97) * mm]});
            skFitSpline(sketch, "E386", {"points": [v(-9.6, -8.97) * mm, v(-9.74, -8.87) * mm, v(-10.12, -8.64) * mm, v(-10.74, -8.3) * mm]});
            skFitSpline(sketch, "E387", {"points": [v(-10.74, -8.3) * mm, v(-11.36, -7.94) * mm, v(-11.8, -7.66) * mm, v(-12.06, -7.46) * mm]});
            skFitSpline(sketch, "E388", {"points": [v(-12.06, -7.46) * mm, v(-12.32, -7.25) * mm, v(-12.51, -7.02) * mm, v(-12.65, -6.77) * mm]});
            skFitSpline(sketch, "E389", {"points": [v(-12.65, -6.77) * mm, v(-12.78, -6.52) * mm, v(-12.85, -6.25) * mm, v(-12.85, -5.95) * mm]});
            skFitSpline(sketch, "E390", {"points": [v(-12.85, -5.95) * mm, v(-12.85, -5.42) * mm, v(-12.65, -4.97) * mm, v(-12.26, -4.6) * mm]});
            skFitSpline(sketch, "E391", {"points": [v(-12.26, -4.6) * mm, v(-11.86, -4.22) * mm, v(-11.35, -4.03) * mm, v(-10.74, -4.03) * mm]});
            skFitSpline(sketch, "E392", {"points": [v(-10.74, -4.03) * mm, v(-10.35, -4.03) * mm, v(-9.95, -4.13) * mm, v(-9.52, -4.32) * mm]});
            skFitSpline(sketch, "E393", {"points": [v(-9.52, -4.32) * mm, v(-9.32, -4.4) * mm, v(-9.18, -4.45) * mm, v(-9.1, -4.45) * mm]});
            skFitSpline(sketch, "E394", {"points": [v(-9.1, -4.45) * mm, v(-9, -4.45) * mm, v(-8.93, -4.42) * mm, v(-8.87, -4.37) * mm]});
            skFitSpline(sketch, "E395", {"points": [v(-8.87, -4.37) * mm, v(-8.81, -4.31) * mm, v(-8.77, -4.2) * mm, v(-8.73, -4.03) * mm]});
            skLineSegment(sketch, "E396", {"start": v(-12.59, -11.63) * mm, "end": v(-12.78, -11.63) * mm});
            skLineSegment(sketch, "E397", {"start": v(-12.78, -11.63) * mm, "end": v(-12.78, -9.14) * mm});
            skLineSegment(sketch, "E398", {"start": v(-12.78, -9.14) * mm, "end": v(-12.59, -9.14) * mm});
            skLineSegment(sketch, "E399", {"start": v(-8.73, -4.03) * mm, "end": v(-8.53, -4.03) * mm});
            skLineSegment(sketch, "E400", {"start": v(-10.03, -3.63) * mm, "end": v(-11, -3.63) * mm});
            skLineSegment(sketch, "E401", {"start": v(-11, -3.63) * mm, "end": v(-12.02, -1.86) * mm});
            skLineSegment(sketch, "E402", {"start": v(-12.02, -1.86) * mm, "end": v(-11.86, -1.86) * mm});
            skLineSegment(sketch, "E403", {"start": v(-11.86, -1.86) * mm, "end": v(-10.4, -3) * mm});
            skLineSegment(sketch, "E404", {"start": v(-10.4, -3) * mm, "end": v(-9.18, -1.86) * mm});
            skLineSegment(sketch, "E405", {"start": v(-9.18, -1.86) * mm, "end": v(-9.02, -1.86) * mm});
            skLineSegment(sketch, "E406", {"start": v(-9.02, -1.86) * mm, "end": v(-10.03, -3.63) * mm});
            skFitSpline(sketch, "E407", {"points": [v(-0.9, -6.5) * mm, v(-1.12, -5.76) * mm, v(-1.43, -5.23) * mm, v(-1.84, -4.9) * mm]});
            skFitSpline(sketch, "E408", {"points": [v(-1.84, -4.9) * mm, v(-2.25, -4.58) * mm, v(-2.74, -4.42) * mm, v(-3.31, -4.42) * mm]});
            skFitSpline(sketch, "E409", {"points": [v(-3.31, -4.42) * mm, v(-3.79, -4.42) * mm, v(-4.22, -4.54) * mm, v(-4.6, -4.79) * mm]});
            skFitSpline(sketch, "E410", {"points": [v(-4.6, -4.79) * mm, v(-5, -5.03) * mm, v(-5.3, -5.42) * mm, v(-5.52, -5.96) * mm]});
            skFitSpline(sketch, "E411", {"points": [v(-5.52, -5.96) * mm, v(-5.74, -6.5) * mm, v(-5.86, -7.16) * mm, v(-5.86, -7.96) * mm]});
            skFitSpline(sketch, "E412", {"points": [v(-5.86, -7.96) * mm, v(-5.86, -8.61) * mm, v(-5.75, -9.18) * mm, v(-5.54, -9.67) * mm]});
            skFitSpline(sketch, "E413", {"points": [v(-5.54, -9.67) * mm, v(-5.33, -10.15) * mm, v(-5.02, -10.52) * mm, v(-4.6, -10.78) * mm]});
            skFitSpline(sketch, "E414", {"points": [v(-4.6, -10.78) * mm, v(-4.18, -11.03) * mm, v(-3.7, -11.16) * mm, v(-3.16, -11.16) * mm]});
            skFitSpline(sketch, "E415", {"points": [v(-3.16, -11.16) * mm, v(-2.69, -11.16) * mm, v(-2.27, -11.06) * mm, v(-1.92, -10.86) * mm]});
            skFitSpline(sketch, "E416", {"points": [v(-1.92, -10.86) * mm, v(-1.56, -10.66) * mm, v(-1.16, -10.26) * mm, v(-0.73, -9.65) * mm]});
            skLineSegment(sketch, "E417", {"start": v(-0.9, -4.03) * mm, "end": v(-0.73, -6.5) * mm});
            skLineSegment(sketch, "E418", {"start": v(-0.73, -6.5) * mm, "end": v(-0.9, -6.5) * mm});
            skFitSpline(sketch, "E419", {"points": [v(-0.57, -9.76) * mm, v(-0.93, -10.4) * mm, v(-1.35, -10.88) * mm, v(-1.84, -11.18) * mm]});
            skFitSpline(sketch, "E420", {"points": [v(-1.84, -11.18) * mm, v(-2.32, -11.48) * mm, v(-2.9, -11.63) * mm, v(-3.56, -11.63) * mm]});
            skFitSpline(sketch, "E421", {"points": [v(-3.56, -11.63) * mm, v(-4.75, -11.63) * mm, v(-5.68, -11.19) * mm, v(-6.33, -10.3) * mm]});
            skFitSpline(sketch, "E422", {"points": [v(-6.33, -10.3) * mm, v(-6.82, -9.63) * mm, v(-7.07, -8.85) * mm, v(-7.07, -7.95) * mm]});
            skFitSpline(sketch, "E423", {"points": [v(-7.07, -7.95) * mm, v(-7.07, -7.22) * mm, v(-6.9, -6.55) * mm, v(-6.59, -5.95) * mm]});
            skFitSpline(sketch, "E424", {"points": [v(-6.59, -5.95) * mm, v(-6.26, -5.34) * mm, v(-5.82, -4.87) * mm, v(-5.25, -4.53) * mm]});
            skFitSpline(sketch, "E425", {"points": [v(-5.25, -4.53) * mm, v(-4.69, -4.2) * mm, v(-4.07, -4.03) * mm, v(-3.4, -4.03) * mm]});
            skFitSpline(sketch, "E426", {"points": [v(-3.4, -4.03) * mm, v(-2.87, -4.03) * mm, v(-2.36, -4.16) * mm, v(-1.85, -4.42) * mm]});
            skFitSpline(sketch, "E427", {"points": [v(-1.85, -4.42) * mm, v(-1.7, -4.5) * mm, v(-1.6, -4.54) * mm, v(-1.53, -4.54) * mm]});
            skFitSpline(sketch, "E428", {"points": [v(-1.53, -4.54) * mm, v(-1.44, -4.54) * mm, v(-1.35, -4.5) * mm, v(-1.28, -4.43) * mm]});
            skFitSpline(sketch, "E429", {"points": [v(-1.28, -4.43) * mm, v(-1.19, -4.34) * mm, v(-1.12, -4.2) * mm, v(-1.08, -4.03) * mm]});
            skLineSegment(sketch, "E430", {"start": v(-0.73, -9.65) * mm, "end": v(-0.57, -9.76) * mm});
            skLineSegment(sketch, "E431", {"start": v(-1.08, -4.03) * mm, "end": v(-0.9, -4.03) * mm});
            skLineSegment(sketch, "E432", {"start": v(-2.94, -3.63) * mm, "end": v(-3.92, -3.63) * mm});
            skLineSegment(sketch, "E433", {"start": v(-3.92, -3.63) * mm, "end": v(-4.93, -1.86) * mm});
            skLineSegment(sketch, "E434", {"start": v(-4.93, -1.86) * mm, "end": v(-4.76, -1.86) * mm});
            skLineSegment(sketch, "E435", {"start": v(-4.76, -1.86) * mm, "end": v(-3.31, -3) * mm});
            skLineSegment(sketch, "E436", {"start": v(-3.31, -3) * mm, "end": v(-2.1, -1.86) * mm});
            skLineSegment(sketch, "E437", {"start": v(-2.1, -1.86) * mm, "end": v(-1.93, -1.86) * mm});
            skLineSegment(sketch, "E438", {"start": v(-1.93, -1.86) * mm, "end": v(-2.94, -3.63) * mm});
            skFitSpline(sketch, "E439", {"points": [v(1.1, -10.18) * mm, v(0.97, -10.46) * mm, v(0.91, -10.67) * mm, v(0.91, -10.81) * mm]});
            skFitSpline(sketch, "E440", {"points": [v(0.91, -10.81) * mm, v(0.91, -10.92) * mm, v(0.96, -11.02) * mm, v(1.07, -11.1) * mm]});
            skFitSpline(sketch, "E441", {"points": [v(1.07, -11.1) * mm, v(1.17, -11.19) * mm, v(1.4, -11.24) * mm, v(1.75, -11.27) * mm]});
            skLineSegment(sketch, "E442", {"start": v(4.38, -9.03) * mm, "end": v(1.58, -9.03) * mm});
            skLineSegment(sketch, "E443", {"start": v(1.58, -9.03) * mm, "end": v(1.1, -10.18) * mm});
            skFitSpline(sketch, "E444", {"points": [v(-0.53, -11.27) * mm, v(-0.23, -11.21) * mm, v(-0.03, -11.15) * mm, v(0.06, -11.06) * mm]});
            skFitSpline(sketch, "E445", {"points": [v(0.06, -11.06) * mm, v(0.24, -10.89) * mm, v(0.44, -10.54) * mm, v(0.66, -10.01) * mm]});
            skLineSegment(sketch, "E446", {"start": v(1.75, -11.27) * mm, "end": v(1.75, -11.47) * mm});
            skLineSegment(sketch, "E447", {"start": v(1.75, -11.47) * mm, "end": v(-0.53, -11.47) * mm});
            skLineSegment(sketch, "E448", {"start": v(-0.53, -11.47) * mm, "end": v(-0.53, -11.27) * mm});
            skFitSpline(sketch, "E449", {"points": [v(5.9, -10.08) * mm, v(6.1, -10.56) * mm, v(6.29, -10.88) * mm, v(6.45, -11.02) * mm]});
            skFitSpline(sketch, "E450", {"points": [v(6.45, -11.02) * mm, v(6.62, -11.17) * mm, v(6.85, -11.25) * mm, v(7.14, -11.27) * mm]});
            skLineSegment(sketch, "E451", {"start": v(0.66, -10.01) * mm, "end": v(3.2, -4.03) * mm});
            skLineSegment(sketch, "E452", {"start": v(3.2, -4.03) * mm, "end": v(3.39, -4.03) * mm});
            skLineSegment(sketch, "E453", {"start": v(3.39, -4.03) * mm, "end": v(5.9, -10.08) * mm});
            skFitSpline(sketch, "E454", {"points": [v(4.3, -11.27) * mm, v(4.58, -11.25) * mm, v(4.77, -11.2) * mm, v(4.87, -11.12) * mm]});
            skFitSpline(sketch, "E455", {"points": [v(4.87, -11.12) * mm, v(4.98, -11.04) * mm, v(5.03, -10.94) * mm, v(5.03, -10.82) * mm]});
            skFitSpline(sketch, "E456", {"points": [v(5.03, -10.82) * mm, v(5.03, -10.67) * mm, v(4.96, -10.42) * mm, v(4.81, -10.08) * mm]});
            skLineSegment(sketch, "E457", {"start": v(7.14, -11.27) * mm, "end": v(7.14, -11.47) * mm});
            skLineSegment(sketch, "E458", {"start": v(7.14, -11.47) * mm, "end": v(4.3, -11.47) * mm});
            skLineSegment(sketch, "E459", {"start": v(4.3, -11.47) * mm, "end": v(4.3, -11.27) * mm});
            skLineSegment(sketch, "E460", {"start": v(4.81, -10.08) * mm, "end": v(4.38, -9.03) * mm});
            skLineSegment(sketch, "E461", {"start": v(4.23, -8.64) * mm, "end": v(3, -5.7) * mm});
            skLineSegment(sketch, "E462", {"start": v(3, -5.7) * mm, "end": v(1.75, -8.64) * mm});
            skLineSegment(sketch, "E463", {"start": v(1.75, -8.64) * mm, "end": v(4.23, -8.64) * mm});
            skFitSpline(sketch, "E464", {"points": [v(13.46, -4.4) * mm, v(13.2, -4.44) * mm, v(13.01, -4.53) * mm, v(12.88, -4.64) * mm]});
            skFitSpline(sketch, "E465", {"points": [v(12.88, -4.64) * mm, v(12.7, -4.82) * mm, v(12.52, -5.09) * mm, v(12.38, -5.45) * mm]});
            skLineSegment(sketch, "E466", {"start": v(13.46, -4.2) * mm, "end": v(13.46, -4.4) * mm});
            skFitSpline(sketch, "E467", {"points": [v(6.96, -5.37) * mm, v(6.82, -5.05) * mm, v(6.72, -4.85) * mm, v(6.67, -4.78) * mm]});
            skFitSpline(sketch, "E468", {"points": [v(6.67, -4.78) * mm, v(6.58, -4.67) * mm, v(6.47, -4.58) * mm, v(6.34, -4.52) * mm]});
            skFitSpline(sketch, "E469", {"points": [v(6.34, -4.52) * mm, v(6.2, -4.45) * mm, v(6.03, -4.41) * mm, v(5.81, -4.4) * mm]});
            skLineSegment(sketch, "E470", {"start": v(12.38, -5.45) * mm, "end": v(9.86, -11.63) * mm});
            skLineSegment(sketch, "E471", {"start": v(9.86, -11.63) * mm, "end": v(9.66, -11.63) * mm});
            skLineSegment(sketch, "E472", {"start": v(9.66, -11.63) * mm, "end": v(6.96, -5.37) * mm});
            skFitSpline(sketch, "E473", {"points": [v(8.76, -4.4) * mm, v(8.43, -4.43) * mm, v(8.21, -4.49) * mm, v(8.11, -4.57) * mm]});
            skFitSpline(sketch, "E474", {"points": [v(8.11, -4.57) * mm, v(8.01, -4.65) * mm, v(7.97, -4.76) * mm, v(7.97, -4.88) * mm]});
            skFitSpline(sketch, "E475", {"points": [v(7.97, -4.88) * mm, v(7.97, -5.06) * mm, v(8.05, -5.34) * mm, v(8.21, -5.72) * mm]});
            skLineSegment(sketch, "E476", {"start": v(5.81, -4.4) * mm, "end": v(5.81, -4.2) * mm});
            skLineSegment(sketch, "E477", {"start": v(5.81, -4.2) * mm, "end": v(8.76, -4.2) * mm});
            skLineSegment(sketch, "E478", {"start": v(8.76, -4.2) * mm, "end": v(8.76, -4.4) * mm});
            skFitSpline(sketch, "E479", {"points": [v(11.75, -5.77) * mm, v(11.92, -5.36) * mm, v(12, -5.07) * mm, v(12, -4.91) * mm]});
            skFitSpline(sketch, "E480", {"points": [v(12, -4.91) * mm, v(12, -4.8) * mm, v(11.95, -4.7) * mm, v(11.85, -4.61) * mm]});
            skFitSpline(sketch, "E481", {"points": [v(11.85, -4.61) * mm, v(11.74, -4.52) * mm, v(11.57, -4.45) * mm, v(11.33, -4.41) * mm]});
            skFitSpline(sketch, "E482", {"points": [v(11.33, -4.41) * mm, v(11.3, -4.4) * mm, v(11.28, -4.4) * mm, v(11.23, -4.4) * mm]});
            skLineSegment(sketch, "E483", {"start": v(8.21, -5.72) * mm, "end": v(10.05, -9.98) * mm});
            skLineSegment(sketch, "E484", {"start": v(10.05, -9.98) * mm, "end": v(11.75, -5.77) * mm});
            skLineSegment(sketch, "E485", {"start": v(11.23, -4.4) * mm, "end": v(11.23, -4.2) * mm});
            skLineSegment(sketch, "E486", {"start": v(11.23, -4.2) * mm, "end": v(13.46, -4.2) * mm});
            skFitSpline(sketch, "E487", {"points": [v(13.76, -10.18) * mm, v(13.64, -10.46) * mm, v(13.58, -10.67) * mm, v(13.58, -10.81) * mm]});
            skFitSpline(sketch, "E488", {"points": [v(13.58, -10.81) * mm, v(13.58, -10.92) * mm, v(13.63, -11.02) * mm, v(13.73, -11.1) * mm]});
            skFitSpline(sketch, "E489", {"points": [v(13.73, -11.1) * mm, v(13.84, -11.19) * mm, v(14.06, -11.24) * mm, v(14.41, -11.27) * mm]});
            skLineSegment(sketch, "E490", {"start": v(17.04, -9.03) * mm, "end": v(14.25, -9.03) * mm});
            skLineSegment(sketch, "E491", {"start": v(14.25, -9.03) * mm, "end": v(13.76, -10.18) * mm});
            skFitSpline(sketch, "E492", {"points": [v(12.14, -11.27) * mm, v(12.44, -11.21) * mm, v(12.64, -11.15) * mm, v(12.72, -11.06) * mm]});
            skFitSpline(sketch, "E493", {"points": [v(12.72, -11.06) * mm, v(12.9, -10.89) * mm, v(13.1, -10.54) * mm, v(13.33, -10.01) * mm]});
            skLineSegment(sketch, "E494", {"start": v(14.41, -11.27) * mm, "end": v(14.41, -11.47) * mm});
            skLineSegment(sketch, "E495", {"start": v(14.41, -11.47) * mm, "end": v(12.14, -11.47) * mm});
            skLineSegment(sketch, "E496", {"start": v(12.14, -11.47) * mm, "end": v(12.14, -11.27) * mm});
            skFitSpline(sketch, "E497", {"points": [v(18.57, -10.08) * mm, v(18.77, -10.56) * mm, v(18.95, -10.88) * mm, v(19.12, -11.02) * mm]});
            skFitSpline(sketch, "E498", {"points": [v(19.12, -11.02) * mm, v(19.28, -11.17) * mm, v(19.51, -11.25) * mm, v(19.8, -11.27) * mm]});
            skLineSegment(sketch, "E499", {"start": v(13.33, -10.01) * mm, "end": v(15.87, -4.03) * mm});
            skLineSegment(sketch, "E500", {"start": v(15.87, -4.03) * mm, "end": v(16.05, -4.03) * mm});
            skLineSegment(sketch, "E501", {"start": v(16.05, -4.03) * mm, "end": v(18.57, -10.08) * mm});
            skFitSpline(sketch, "E502", {"points": [v(16.96, -11.27) * mm, v(17.24, -11.25) * mm, v(17.44, -11.2) * mm, v(17.54, -11.12) * mm]});
            skFitSpline(sketch, "E503", {"points": [v(17.54, -11.12) * mm, v(17.64, -11.04) * mm, v(17.7, -10.94) * mm, v(17.7, -10.82) * mm]});
            skFitSpline(sketch, "E504", {"points": [v(17.7, -10.82) * mm, v(17.7, -10.67) * mm, v(17.62, -10.42) * mm, v(17.48, -10.08) * mm]});
            skLineSegment(sketch, "E505", {"start": v(19.8, -11.27) * mm, "end": v(19.8, -11.47) * mm});
            skLineSegment(sketch, "E506", {"start": v(19.8, -11.47) * mm, "end": v(16.96, -11.47) * mm});
            skLineSegment(sketch, "E507", {"start": v(16.96, -11.47) * mm, "end": v(16.96, -11.27) * mm});
            skLineSegment(sketch, "E508", {"start": v(17.48, -10.08) * mm, "end": v(17.04, -9.03) * mm});
            skLineSegment(sketch, "E509", {"start": v(16.9, -8.64) * mm, "end": v(15.67, -5.7) * mm});
            skLineSegment(sketch, "E510", {"start": v(15.67, -5.7) * mm, "end": v(14.41, -8.64) * mm});
            skLineSegment(sketch, "E511", {"start": v(14.41, -8.64) * mm, "end": v(16.9, -8.64) * mm});
            skFitSpline(sketch, "E512", {"points": [v(22.93, -8.07) * mm, v(22.75, -8.08) * mm, v(22.6, -8.08) * mm, v(22.49, -8.08) * mm]});
            skFitSpline(sketch, "E513", {"points": [v(22.49, -8.08) * mm, v(22.44, -8.08) * mm, v(22.4, -8.08) * mm, v(22.34, -8.08) * mm]});
            skFitSpline(sketch, "E514", {"points": [v(22.34, -8.08) * mm, v(22.29, -8.07) * mm, v(22.23, -8.07) * mm, v(22.18, -8.07) * mm]});
            skLineSegment(sketch, "E515", {"start": v(27.3, -11.47) * mm, "end": v(25.38, -11.47) * mm});
            skLineSegment(sketch, "E516", {"start": v(25.38, -11.47) * mm, "end": v(22.93, -8.07) * mm});
            skFitSpline(sketch, "E517", {"points": [v(22.18, -10.18) * mm, v(22.18, -10.64) * mm, v(22.23, -10.92) * mm, v(22.32, -11.03) * mm]});
            skFitSpline(sketch, "E518", {"points": [v(22.32, -11.03) * mm, v(22.46, -11.19) * mm, v(22.66, -11.27) * mm, v(22.93, -11.27) * mm]});
            skLineSegment(sketch, "E519", {"start": v(22.18, -8.07) * mm, "end": v(22.18, -10.18) * mm});
            skFitSpline(sketch, "E520", {"points": [v(20.4, -11.27) * mm, v(20.7, -11.27) * mm, v(20.92, -11.17) * mm, v(21.05, -10.97) * mm]});
            skFitSpline(sketch, "E521", {"points": [v(21.05, -10.97) * mm, v(21.12, -10.86) * mm, v(21.16, -10.6) * mm, v(21.16, -10.18) * mm]});
            skLineSegment(sketch, "E522", {"start": v(22.93, -11.27) * mm, "end": v(23.21, -11.27) * mm});
            skLineSegment(sketch, "E523", {"start": v(23.21, -11.27) * mm, "end": v(23.21, -11.47) * mm});
            skLineSegment(sketch, "E524", {"start": v(23.21, -11.47) * mm, "end": v(20.12, -11.47) * mm});
            skLineSegment(sketch, "E525", {"start": v(20.12, -11.47) * mm, "end": v(20.12, -11.27) * mm});
            skLineSegment(sketch, "E526", {"start": v(20.12, -11.27) * mm, "end": v(20.4, -11.27) * mm});
            skFitSpline(sketch, "E527", {"points": [v(21.16, -5.48) * mm, v(21.16, -5.03) * mm, v(21.1, -4.74) * mm, v(21, -4.63) * mm]});
            skFitSpline(sketch, "E528", {"points": [v(21, -4.63) * mm, v(20.87, -4.48) * mm, v(20.67, -4.4) * mm, v(20.4, -4.4) * mm]});
            skLineSegment(sketch, "E529", {"start": v(21.16, -10.18) * mm, "end": v(21.16, -5.48) * mm});
            skFitSpline(sketch, "E530", {"points": [v(22.75, -4.2) * mm, v(23.52, -4.2) * mm, v(24.08, -4.25) * mm, v(24.45, -4.37) * mm]});
            skFitSpline(sketch, "E531", {"points": [v(24.45, -4.37) * mm, v(24.81, -4.48) * mm, v(25.12, -4.69) * mm, v(25.37, -4.99) * mm]});
            skFitSpline(sketch, "E532", {"points": [v(25.37, -4.99) * mm, v(25.63, -5.3) * mm, v(25.75, -5.65) * mm, v(25.75, -6.07) * mm]});
            skFitSpline(sketch, "E533", {"points": [v(25.75, -6.07) * mm, v(25.75, -6.52) * mm, v(25.6, -6.9) * mm, v(25.32, -7.23) * mm]});
            skFitSpline(sketch, "E534", {"points": [v(25.32, -7.23) * mm, v(25.03, -7.56) * mm, v(24.58, -7.8) * mm, v(23.98, -7.93) * mm]});
            skLineSegment(sketch, "E535", {"start": v(20.4, -4.4) * mm, "end": v(20.12, -4.4) * mm});
            skLineSegment(sketch, "E536", {"start": v(20.12, -4.4) * mm, "end": v(20.12, -4.2) * mm});
            skLineSegment(sketch, "E537", {"start": v(20.12, -4.2) * mm, "end": v(22.75, -4.2) * mm});
            skFitSpline(sketch, "E538", {"points": [v(25.47, -10.01) * mm, v(25.8, -10.5) * mm, v(26.1, -10.81) * mm, v(26.34, -10.97) * mm]});
            skFitSpline(sketch, "E539", {"points": [v(26.34, -10.97) * mm, v(26.59, -11.13) * mm, v(26.9, -11.23) * mm, v(27.3, -11.27) * mm]});
            skLineSegment(sketch, "E540", {"start": v(23.98, -7.93) * mm, "end": v(25.47, -10.01) * mm});
            skFitSpline(sketch, "E541", {"points": [v(22.18, -7.73) * mm, v(22.24, -7.73) * mm, v(22.3, -7.73) * mm, v(22.35, -7.73) * mm]});
            skFitSpline(sketch, "E542", {"points": [v(22.35, -7.73) * mm, v(22.4, -7.73) * mm, v(22.44, -7.74) * mm, v(22.47, -7.74) * mm]});
            skFitSpline(sketch, "E543", {"points": [v(22.47, -7.74) * mm, v(23.16, -7.74) * mm, v(23.68, -7.59) * mm, v(24.03, -7.29) * mm]});
            skFitSpline(sketch, "E544", {"points": [v(24.03, -7.29) * mm, v(24.38, -6.99) * mm, v(24.56, -6.6) * mm, v(24.56, -6.14) * mm]});
            skFitSpline(sketch, "E545", {"points": [v(24.56, -6.14) * mm, v(24.56, -5.68) * mm, v(24.41, -5.32) * mm, v(24.13, -5.03) * mm]});
            skFitSpline(sketch, "E546", {"points": [v(24.13, -5.03) * mm, v(23.85, -4.75) * mm, v(23.48, -4.6) * mm, v(23.01, -4.6) * mm]});
            skFitSpline(sketch, "E547", {"points": [v(23.01, -4.6) * mm, v(22.8, -4.6) * mm, v(22.53, -4.64) * mm, v(22.18, -4.7) * mm]});
            skLineSegment(sketch, "E548", {"start": v(27.3, -11.27) * mm, "end": v(27.3, -11.47) * mm});
            skLineSegment(sketch, "E549", {"start": v(22.18, -4.7) * mm, "end": v(22.18, -7.73) * mm});
            skSolve(sketch);
        }
        {
            var Q0;
            Q0=qSketchRegion(id+"F0",true);
            extrude(context, id + "F1", {"entities" : qUnion([Q0]), "depth" : 2 * mm, "offsetDistance" : 25 * mm});
        }
        {
            var Q0;
            Q0=makeQuery(id+"F1.opExtrude","CAP_FACE",FACE,{"disambiguationData":[OSD([sQuery(id+"F0.wireOp",EDGE,"E153"),sQuery(id+"F0.wireOp",EDGE,"E154"),sQuery(id+"F0.wireOp",EDGE,"E155"),sQuery(id+"F0.wireOp",EDGE,"E156"),sQuery(id+"F0.wireOp",EDGE,"E157"),sQuery(id+"F0.wireOp",EDGE,"E158"),sQuery(id+"F0.wireOp",EDGE,"E159"),sQuery(id+"F0.wireOp",EDGE,"E160"),sQuery(id+"F0.wireOp",EDGE,"E161"),sQuery(id+"F0.wireOp",EDGE,"E162"),sQuery(id+"F0.wireOp",EDGE,"E163"),sQuery(id+"F0.wireOp",EDGE,"E164"),sQuery(id+"F0.wireOp",EDGE,"E165"),sQuery(id+"F0.wireOp",EDGE,"E166"),sQuery(id+"F0.wireOp",EDGE,"E167"),sQuery(id+"F0.wireOp",EDGE,"E169"),sQuery(id+"F0.wireOp",EDGE,"E170"),sQuery(id+"F0.wireOp",EDGE,"E171"),sQuery(id+"F0.wireOp",EDGE,"E172"),sQuery(id+"F0.wireOp",EDGE,"E173"),sQuery(id+"F0.wireOp",EDGE,"E174"),sQuery(id+"F0.wireOp",EDGE,"E175"),sQuery(id+"F0.wireOp",EDGE,"E176"),sQuery(id+"F0.wireOp",EDGE,"E177"),sQuery(id+"F0.wireOp",EDGE,"E178"),sQuery(id+"F0.wireOp",EDGE,"E179"),sQuery(id+"F0.wireOp",EDGE,"E180"),sQuery(id+"F0.wireOp",EDGE,"E181"),sQuery(id+"F0.wireOp",EDGE,"E182"),sQuery(id+"F0.wireOp",EDGE,"E183"),sQuery(id+"F0.wireOp",EDGE,"E184"),sQuery(id+"F0.wireOp",EDGE,"E185"),sQuery(id+"F0.wireOp",EDGE,"E186"),sQuery(id+"F0.wireOp",EDGE,"E187"),sQuery(id+"F0.wireOp",EDGE,"E188"),sQuery(id+"F0.wireOp",EDGE,"E189"),sQuery(id+"F0.wireOp",EDGE,"E190"),sQuery(id+"F0.wireOp",EDGE,"E191"),sQuery(id+"F0.wireOp",EDGE,"E192"),sQuery(id+"F0.wireOp",EDGE,"E193"),sQuery(id+"F0.wireOp",EDGE,"E194"),sQuery(id+"F0.wireOp",EDGE,"E195"),sQuery(id+"F0.wireOp",EDGE,"E196"),sQuery(id+"F0.wireOp",EDGE,"E197"),sQuery(id+"F0.wireOp",EDGE,"E198"),sQuery(id+"F0.wireOp",EDGE,"E199"),sQuery(id+"F0.wireOp",EDGE,"E200"),sQuery(id+"F0.wireOp",EDGE,"E201"),sQuery(id+"F0.wireOp",EDGE,"E202"),sQuery(id+"F0.wireOp",EDGE,"E203"),sQuery(id+"F0.wireOp",EDGE,"E204"),sQuery(id+"F0.wireOp",EDGE,"E205"),sQuery(id+"F0.wireOp",EDGE,"E206"),sQuery(id+"F0.wireOp",EDGE,"E207"),sQuery(id+"F0.wireOp",EDGE,"E208"),sQuery(id+"F0.wireOp",EDGE,"E209"),sQuery(id+"F0.wireOp",EDGE,"E210"),sQuery(id+"F0.wireOp",EDGE,"E211"),sQuery(id+"F0.wireOp",EDGE,"E58"),sQuery(id+"F0.wireOp",EDGE,"E59"),sQuery(id+"F0.wireOp",EDGE,"E212"),sQuery(id+"F0.wireOp",EDGE,"E213"),sQuery(id+"F0.wireOp",EDGE,"E214"),sQuery(id+"F0.wireOp",EDGE,"E215"),sQuery(id+"F0.wireOp",EDGE,"E216"),sQuery(id+"F0.wireOp",EDGE,"E217"),sQuery(id+"F0.wireOp",EDGE,"E218"),sQuery(id+"F0.wireOp",EDGE,"E219"),sQuery(id+"F0.wireOp",EDGE,"E68"),sQuery(id+"F0.wireOp",EDGE,"E69"),sQuery(id+"F0.wireOp",EDGE,"E220"),sQuery(id+"F0.wireOp",EDGE,"E221"),sQuery(id+"F0.wireOp",EDGE,"E222"),sQuery(id+"F0.wireOp",EDGE,"E223"),sQuery(id+"F0.wireOp",EDGE,"E224"),sQuery(id+"F0.wireOp",EDGE,"E225"),sQuery(id+"F0.wireOp",EDGE,"E77"),sQuery(id+"F0.wireOp",EDGE,"E78"),sQuery(id+"F0.wireOp",EDGE,"E226"),sQuery(id+"F0.wireOp",EDGE,"E227"),sQuery(id+"F0.wireOp",EDGE,"E81"),sQuery(id+"F0.wireOp",EDGE,"E82"),sQuery(id+"F0.wireOp",EDGE,"E228"),sQuery(id+"F0.wireOp",EDGE,"E229"),sQuery(id+"F0.wireOp",EDGE,"E230"),sQuery(id+"F0.wireOp",EDGE,"E231"),sQuery(id+"F0.wireOp",EDGE,"E232"),sQuery(id+"F0.wireOp",EDGE,"E233"),sQuery(id+"F0.wireOp",EDGE,"E234"),sQuery(id+"F0.wireOp",EDGE,"E235"),sQuery(id+"F0.wireOp",EDGE,"E236"),sQuery(id+"F0.wireOp",EDGE,"E237"),sQuery(id+"F0.wireOp",EDGE,"E238"),sQuery(id+"F0.wireOp",EDGE,"E239"),sQuery(id+"F0.wireOp",EDGE,"E240"),sQuery(id+"F0.wireOp",EDGE,"E241"),sQuery(id+"F0.wireOp",EDGE,"E242"),sQuery(id+"F0.wireOp",EDGE,"E243"),sQuery(id+"F0.wireOp",EDGE,"E99"),sQuery(id+"F0.wireOp",EDGE,"E100"),sQuery(id+"F0.wireOp",EDGE,"E244"),sQuery(id+"F0.wireOp",EDGE,"E245"),sQuery(id+"F0.wireOp",EDGE,"E246"),sQuery(id+"F0.wireOp",EDGE,"E247"),sQuery(id+"F0.wireOp",EDGE,"E248"),sQuery(id+"F0.wireOp",EDGE,"E249"),sQuery(id+"F0.wireOp",EDGE,"E250"),sQuery(id+"F0.wireOp",EDGE,"E251"),sQuery(id+"F0.wireOp",EDGE,"E252"),sQuery(id+"F0.wireOp",EDGE,"E253"),sQuery(id+"F0.wireOp",EDGE,"E254"),sQuery(id+"F0.wireOp",EDGE,"E255"),sQuery(id+"F0.wireOp",EDGE,"E256"),sQuery(id+"F0.wireOp",EDGE,"E257"),sQuery(id+"F0.wireOp",EDGE,"E258"),sQuery(id+"F0.wireOp",EDGE,"E259"),sQuery(id+"F0.wireOp",EDGE,"E260"),sQuery(id+"F0.wireOp",EDGE,"E261"),sQuery(id+"F0.wireOp",EDGE,"E262"),sQuery(id+"F0.wireOp",EDGE,"E263"),sQuery(id+"F0.wireOp",EDGE,"E264"),sQuery(id+"F0.wireOp",EDGE,"E265"),sQuery(id+"F0.wireOp",EDGE,"E266"),sQuery(id+"F0.wireOp",EDGE,"E267"),sQuery(id+"F0.wireOp",EDGE,"E268"),sQuery(id+"F0.wireOp",EDGE,"E269"),sQuery(id+"F0.wireOp",EDGE,"E270"),sQuery(id+"F0.wireOp",EDGE,"E271"),sQuery(id+"F0.wireOp",EDGE,"E272"),sQuery(id+"F0.wireOp",EDGE,"E273"),sQuery(id+"F0.wireOp",EDGE,"E274"),sQuery(id+"F0.wireOp",EDGE,"E275"),sQuery(id+"F0.wireOp",EDGE,"E276"),sQuery(id+"F0.wireOp",EDGE,"E277"),sQuery(id+"F0.wireOp",EDGE,"E278"),sQuery(id+"F0.wireOp",EDGE,"E137"),sQuery(id+"F0.wireOp",EDGE,"E279"),sQuery(id+"F0.wireOp",EDGE,"E280"),sQuery(id+"F0.wireOp",EDGE,"E281"),sQuery(id+"F0.wireOp",EDGE,"E282"),sQuery(id+"F0.wireOp",EDGE,"E283"),sQuery(id+"F0.wireOp",EDGE,"E284"),sQuery(id+"F0.wireOp",EDGE,"E285"),sQuery(id+"F0.wireOp",EDGE,"E286"),sQuery(id+"F0.wireOp",EDGE,"E287"),sQuery(id+"F0.wireOp",EDGE,"E288"),sQuery(id+"F0.wireOp",EDGE,"E289"),sQuery(id+"F0.wireOp",EDGE,"E290"),sQuery(id+"F0.wireOp",EDGE,"E291"),sQuery(id+"F0.wireOp",EDGE,"E292")])],"isStart":true});
            var sketch = newSketch(context, id + "F2", { "sketchPlane" : qUnion([Q0])});
            skLineSegment(sketch, "E550.bottom", {"start": v(-27.66, 12.62) * mm, "end": v(28, 12.62) * mm});
            skLineSegment(sketch, "E550.top", {"start": v(-27.66, -12.47) * mm, "end": v(28, -12.47) * mm});
            skLineSegment(sketch, "E550.left", {"start": v(-27.66, 12.62) * mm, "end": v(-27.66, -12.47) * mm});
            skLineSegment(sketch, "E550.right", {"start": v(28, 12.62) * mm, "end": v(28, -12.47) * mm});
            skSolve(sketch);
        }
        {
            var Q0;
            Q0=qSketchRegion(id+"F2",true);
            extrude(context, id + "F3", {"entities" : qUnion([Q0]), "operationType" : NewBodyOperationType.ADD, "depth" : 1 * mm, "offsetDistance" : 25 * mm});
        }
        {
            var Q0;
            Q0=makeQuery(id+"F1.opExtrude","SWEPT_BODY",BODY,{"disambiguationData":[OSD([sQuery(id+"F0.wireOp",EDGE,"E153"),sQuery(id+"F0.wireOp",EDGE,"E154"),sQuery(id+"F0.wireOp",EDGE,"E155"),sQuery(id+"F0.wireOp",EDGE,"E156"),sQuery(id+"F0.wireOp",EDGE,"E157"),sQuery(id+"F0.wireOp",EDGE,"E158"),sQuery(id+"F0.wireOp",EDGE,"E159"),sQuery(id+"F0.wireOp",EDGE,"E160"),sQuery(id+"F0.wireOp",EDGE,"E161"),sQuery(id+"F0.wireOp",EDGE,"E162"),sQuery(id+"F0.wireOp",EDGE,"E163"),sQuery(id+"F0.wireOp",EDGE,"E164"),sQuery(id+"F0.wireOp",EDGE,"E165"),sQuery(id+"F0.wireOp",EDGE,"E166"),sQuery(id+"F0.wireOp",EDGE,"E167"),sQuery(id+"F0.wireOp",EDGE,"E169"),sQuery(id+"F0.wireOp",EDGE,"E170"),sQuery(id+"F0.wireOp",EDGE,"E171"),sQuery(id+"F0.wireOp",EDGE,"E172"),sQuery(id+"F0.wireOp",EDGE,"E173"),sQuery(id+"F0.wireOp",EDGE,"E174"),sQuery(id+"F0.wireOp",EDGE,"E175"),sQuery(id+"F0.wireOp",EDGE,"E176"),sQuery(id+"F0.wireOp",EDGE,"E177"),sQuery(id+"F0.wireOp",EDGE,"E178"),sQuery(id+"F0.wireOp",EDGE,"E179"),sQuery(id+"F0.wireOp",EDGE,"E180"),sQuery(id+"F0.wireOp",EDGE,"E181"),sQuery(id+"F0.wireOp",EDGE,"E182"),sQuery(id+"F0.wireOp",EDGE,"E183"),sQuery(id+"F0.wireOp",EDGE,"E184"),sQuery(id+"F0.wireOp",EDGE,"E185"),sQuery(id+"F0.wireOp",EDGE,"E186"),sQuery(id+"F0.wireOp",EDGE,"E187"),sQuery(id+"F0.wireOp",EDGE,"E188"),sQuery(id+"F0.wireOp",EDGE,"E189"),sQuery(id+"F0.wireOp",EDGE,"E190"),sQuery(id+"F0.wireOp",EDGE,"E191"),sQuery(id+"F0.wireOp",EDGE,"E192"),sQuery(id+"F0.wireOp",EDGE,"E193"),sQuery(id+"F0.wireOp",EDGE,"E194"),sQuery(id+"F0.wireOp",EDGE,"E195"),sQuery(id+"F0.wireOp",EDGE,"E196"),sQuery(id+"F0.wireOp",EDGE,"E197"),sQuery(id+"F0.wireOp",EDGE,"E198"),sQuery(id+"F0.wireOp",EDGE,"E199"),sQuery(id+"F0.wireOp",EDGE,"E200"),sQuery(id+"F0.wireOp",EDGE,"E201"),sQuery(id+"F0.wireOp",EDGE,"E202"),sQuery(id+"F0.wireOp",EDGE,"E203"),sQuery(id+"F0.wireOp",EDGE,"E204"),sQuery(id+"F0.wireOp",EDGE,"E205"),sQuery(id+"F0.wireOp",EDGE,"E206"),sQuery(id+"F0.wireOp",EDGE,"E207"),sQuery(id+"F0.wireOp",EDGE,"E208"),sQuery(id+"F0.wireOp",EDGE,"E209"),sQuery(id+"F0.wireOp",EDGE,"E210"),sQuery(id+"F0.wireOp",EDGE,"E211"),sQuery(id+"F0.wireOp",EDGE,"E58"),sQuery(id+"F0.wireOp",EDGE,"E59"),sQuery(id+"F0.wireOp",EDGE,"E212"),sQuery(id+"F0.wireOp",EDGE,"E213"),sQuery(id+"F0.wireOp",EDGE,"E214"),sQuery(id+"F0.wireOp",EDGE,"E215"),sQuery(id+"F0.wireOp",EDGE,"E216"),sQuery(id+"F0.wireOp",EDGE,"E217"),sQuery(id+"F0.wireOp",EDGE,"E218"),sQuery(id+"F0.wireOp",EDGE,"E219"),sQuery(id+"F0.wireOp",EDGE,"E68"),sQuery(id+"F0.wireOp",EDGE,"E69"),sQuery(id+"F0.wireOp",EDGE,"E220"),sQuery(id+"F0.wireOp",EDGE,"E221"),sQuery(id+"F0.wireOp",EDGE,"E222"),sQuery(id+"F0.wireOp",EDGE,"E223"),sQuery(id+"F0.wireOp",EDGE,"E224"),sQuery(id+"F0.wireOp",EDGE,"E225"),sQuery(id+"F0.wireOp",EDGE,"E77"),sQuery(id+"F0.wireOp",EDGE,"E78"),sQuery(id+"F0.wireOp",EDGE,"E226"),sQuery(id+"F0.wireOp",EDGE,"E227"),sQuery(id+"F0.wireOp",EDGE,"E81"),sQuery(id+"F0.wireOp",EDGE,"E82"),sQuery(id+"F0.wireOp",EDGE,"E228"),sQuery(id+"F0.wireOp",EDGE,"E229"),sQuery(id+"F0.wireOp",EDGE,"E230"),sQuery(id+"F0.wireOp",EDGE,"E231"),sQuery(id+"F0.wireOp",EDGE,"E232"),sQuery(id+"F0.wireOp",EDGE,"E233"),sQuery(id+"F0.wireOp",EDGE,"E234"),sQuery(id+"F0.wireOp",EDGE,"E235"),sQuery(id+"F0.wireOp",EDGE,"E236"),sQuery(id+"F0.wireOp",EDGE,"E237"),sQuery(id+"F0.wireOp",EDGE,"E238"),sQuery(id+"F0.wireOp",EDGE,"E239"),sQuery(id+"F0.wireOp",EDGE,"E240"),sQuery(id+"F0.wireOp",EDGE,"E241"),sQuery(id+"F0.wireOp",EDGE,"E242"),sQuery(id+"F0.wireOp",EDGE,"E243"),sQuery(id+"F0.wireOp",EDGE,"E99"),sQuery(id+"F0.wireOp",EDGE,"E100"),sQuery(id+"F0.wireOp",EDGE,"E244"),sQuery(id+"F0.wireOp",EDGE,"E245"),sQuery(id+"F0.wireOp",EDGE,"E246"),sQuery(id+"F0.wireOp",EDGE,"E247"),sQuery(id+"F0.wireOp",EDGE,"E248"),sQuery(id+"F0.wireOp",EDGE,"E249"),sQuery(id+"F0.wireOp",EDGE,"E250"),sQuery(id+"F0.wireOp",EDGE,"E251"),sQuery(id+"F0.wireOp",EDGE,"E252"),sQuery(id+"F0.wireOp",EDGE,"E253"),sQuery(id+"F0.wireOp",EDGE,"E254"),sQuery(id+"F0.wireOp",EDGE,"E255"),sQuery(id+"F0.wireOp",EDGE,"E256"),sQuery(id+"F0.wireOp",EDGE,"E257"),sQuery(id+"F0.wireOp",EDGE,"E258"),sQuery(id+"F0.wireOp",EDGE,"E259"),sQuery(id+"F0.wireOp",EDGE,"E260"),sQuery(id+"F0.wireOp",EDGE,"E261"),sQuery(id+"F0.wireOp",EDGE,"E262"),sQuery(id+"F0.wireOp",EDGE,"E263"),sQuery(id+"F0.wireOp",EDGE,"E264"),sQuery(id+"F0.wireOp",EDGE,"E265"),sQuery(id+"F0.wireOp",EDGE,"E266"),sQuery(id+"F0.wireOp",EDGE,"E267"),sQuery(id+"F0.wireOp",EDGE,"E268"),sQuery(id+"F0.wireOp",EDGE,"E269"),sQuery(id+"F0.wireOp",EDGE,"E270"),sQuery(id+"F0.wireOp",EDGE,"E271"),sQuery(id+"F0.wireOp",EDGE,"E272"),sQuery(id+"F0.wireOp",EDGE,"E273"),sQuery(id+"F0.wireOp",EDGE,"E274"),sQuery(id+"F0.wireOp",EDGE,"E275"),sQuery(id+"F0.wireOp",EDGE,"E276"),sQuery(id+"F0.wireOp",EDGE,"E277"),sQuery(id+"F0.wireOp",EDGE,"E278"),sQuery(id+"F0.wireOp",EDGE,"E137"),sQuery(id+"F0.wireOp",EDGE,"E279"),sQuery(id+"F0.wireOp",EDGE,"E280"),sQuery(id+"F0.wireOp",EDGE,"E281"),sQuery(id+"F0.wireOp",EDGE,"E282"),sQuery(id+"F0.wireOp",EDGE,"E283"),sQuery(id+"F0.wireOp",EDGE,"E284"),sQuery(id+"F0.wireOp",EDGE,"E285"),sQuery(id+"F0.wireOp",EDGE,"E286"),sQuery(id+"F0.wireOp",EDGE,"E287"),sQuery(id+"F0.wireOp",EDGE,"E288"),sQuery(id+"F0.wireOp",EDGE,"E289"),sQuery(id+"F0.wireOp",EDGE,"E290"),sQuery(id+"F0.wireOp",EDGE,"E291"),sQuery(id+"F0.wireOp",EDGE,"E292")])]});
            var Q1;
            Q1=makeQuery(id+"F3.opExtrude","SWEPT_FACE",FACE,{"disambiguationData":[OSD([sQuery(id+"F2.wireOp",EDGE,"E550.left")])]});
            mirror(context, id + "F4", {"entities" : qUnion([Q0]), "mirrorPlane" : qUnion([Q1])});
        }
    });
